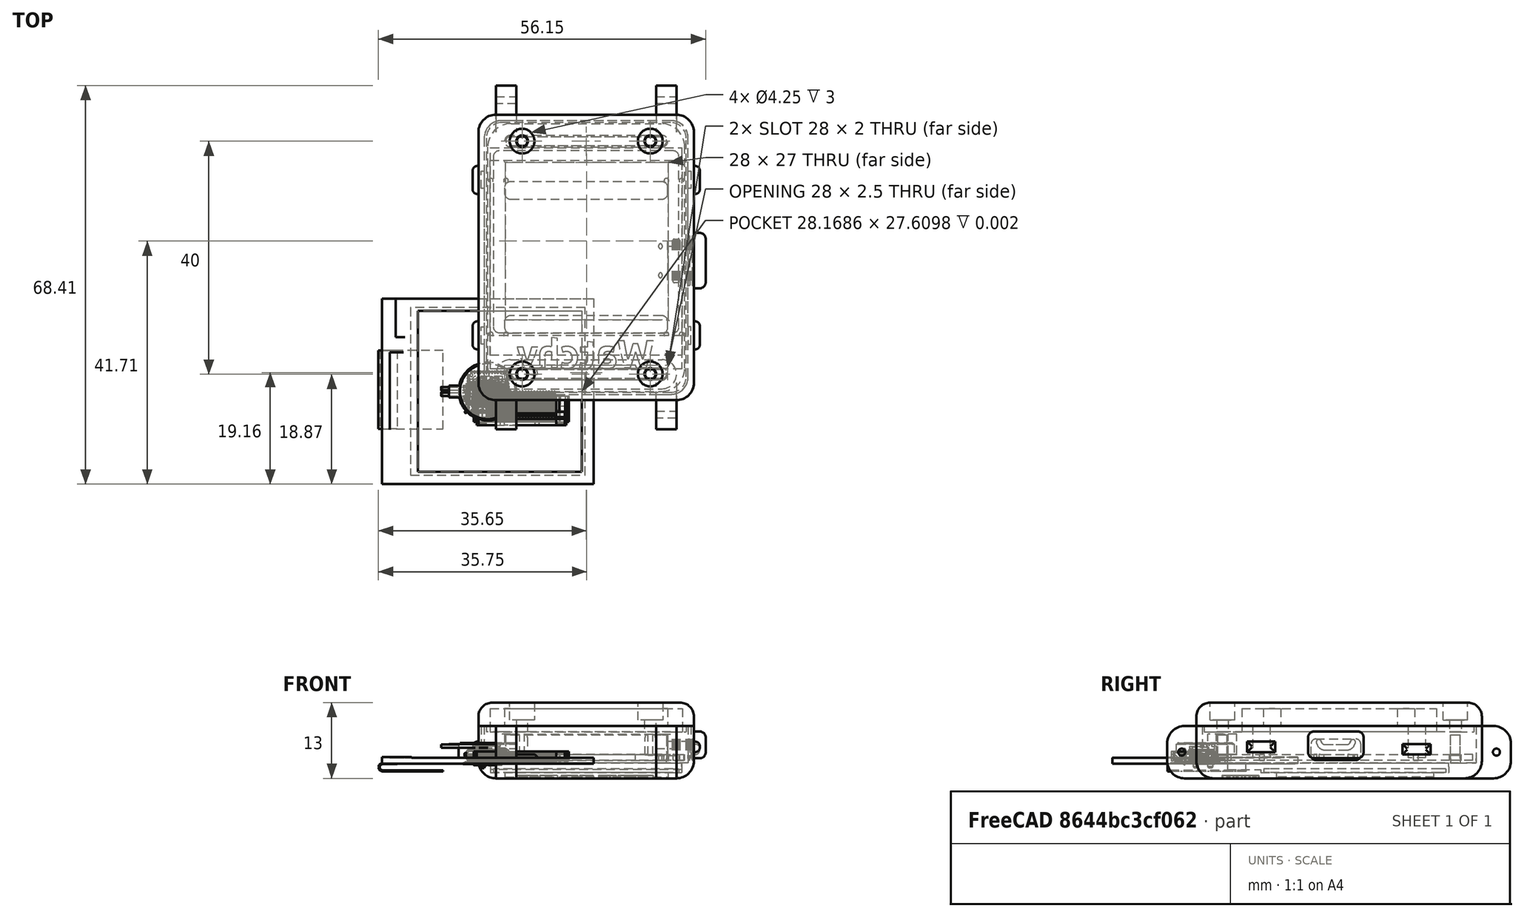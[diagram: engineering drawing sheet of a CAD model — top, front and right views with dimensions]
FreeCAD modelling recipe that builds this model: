
FCSTD DOCUMENT  (FreeCAD 0.20R29177 +426 (Git))
Label: JJ-WATCHY
License: All rights reserved
LicenseURL: http://en.wikipedia.org/wiki/All_rights_reserved
objects: Part::Feature×58, App::Part×56, Sketcher::SketchObject×26, PartDesign::Pad×21, PartDesign::Pocket×14, PartDesign::Fillet×10, PartDesign::ShapeBinder×7, PartDesign::Body×6, PartDesign::Plane×3, Part::Part2DObjectPython×1, Part::Extrusion×1, PartDesign::FeatureBase×1, Mesh::Feature×1, Part::Fuse×1, Part::Cut×1
note: 195 computed .brp shape members not serialized (recipe doc carries the construction recipe); baked Part::Feature solids carry a one-line shape summary decoded from their .brp

FEATURE [Part::Feature] Part__Feature  label="SOLID (15)"
  shape: bbox 7.981 x 5.422 x 2.941 mm, 498 faces (baked)
FEATURE [App::Part] USB_Micro_B_Molex_47346_0001  label="USB_Micro-B_Molex_47346-0001"
  Group = -> [Part__Feature]
  Origin = -> Origin
  Placement = pos=(31.38,22.43,1.65) rot=(0,0,1;1.5708rad)
FEATURE [Part::Feature] Part__Feature001  label="SOLID"
  shape: bbox 1.6 x 0.8 x 0.8 mm, 28 faces (baked)
FEATURE [App::Part] C_0603_1608Metric
  Group = -> [Part__Feature001]
  Origin = -> Origin001
  Placement = pos=(5.16,37.71,1.65) rot=(0,0,1;0rad)
FEATURE [Part::Feature] Part__Feature002  label="SOLID (16)"
  shape: bbox 6.669 x 4.906 x 2.452 mm, 452 faces (baked)
FEATURE [App::Part] Button
  Group = -> [Part__Feature002]
  Origin = -> Origin002
  Placement = pos=(2.38,35.43,1.65) rot=(0,0,-1;1.5708rad)
FEATURE [Part::Feature] Part__Feature003  label="SOLID (16)001"
  shape: bbox 6.669 x 4.906 x 2.452 mm, 452 faces (baked)
FEATURE [App::Part] Button001
  Group = -> [Part__Feature003]
  Origin = -> Origin003
  Placement = pos=(2.38,8.73,1.65) rot=(0,0,-1;1.5708rad)
FEATURE [Part::Feature] Part__Feature004  label="SOLID (16)002"
  shape: bbox 6.669 x 4.906 x 2.452 mm, 452 faces (baked)
FEATURE [App::Part] Button002
  Group = -> [Part__Feature004]
  Origin = -> Origin004
  Placement = pos=(31.42,37.23,1.65) rot=(0,0,1;1.5708rad)
FEATURE [Part::Feature] Part__Feature005  label="SOLID (16)003"
  shape: bbox 6.669 x 4.906 x 2.452 mm, 452 faces (baked)
FEATURE [App::Part] Button003
  Group = -> [Part__Feature005]
  Origin = -> Origin005
  Placement = pos=(31.42,10.53,1.65) rot=(0,0,1;1.5708rad)
FEATURE [Part::Feature] Part__Feature006  label="SOLID (1)"
  shape: bbox 2 x 2 x 1.025 mm, 68 faces (baked)
FEATURE [App::Part] LGA_12_2x2mm_P0_5mm  label="LGA-12_2x2mm_P0.5mm"
  Group = -> [Part__Feature006]
  Origin = -> Origin006
  Placement = pos=(10.76,34.89,1.65) rot=(0,0,1;3.14159rad)
FEATURE [Part::Feature] Part__Feature007  label="COMPOUND (3)"
  shape: bbox 16.3 x 5.85 x 2.11 mm, 1280 faces, 17 solids (baked)
FEATURE [App::Part] FPC_24  label="FPC-24"
  Group = -> [Part__Feature007]
  Origin = -> Origin007
  Placement = pos=(11.025,19.09,1.65) rot=(0,0,1;0rad)
FEATURE [Part::Feature] Part__Feature008  label="SOLID (4)"
  shape: bbox 7.65 x 5.2 x 3.4 mm, 136 faces (baked)
FEATURE [App::Part] Molex_PicoBlade_53261_0271_1x02_1MP_P1_25mm_Horizontal  label="Molex_PicoBlade_53261-0271_1x02-1MP_P1.25mm_Horizontal"
  Group = -> [Part__Feature008]
  Origin = -> Origin008
  Placement = pos=(28.63,31.39,1.65) rot=(0,0,-1;1.5708rad)
FEATURE [Part::Feature] Part__Feature009  label="SOLID (2)"
  shape: bbox 1 x 0.5 x 0.35 mm, 26 faces (baked)
FEATURE [App::Part] R_0402_1005Metric
  Group = -> [Part__Feature009]
  Origin = -> Origin009
  Placement = pos=(31.7,28.28,1.65) rot=(0,0,1;1.5708rad)
FEATURE [Part::Feature] Part__Feature010  label="SOLID (5)"
  shape: bbox 4 x 4 x 1.1 mm, 158 faces (baked)
FEATURE [App::Part] QFN_24_1EP_4x4mm_P0_5mm_EP2_7x2_7mm  label="QFN-24-1EP_4x4mm_P0.5mm_EP2.7x2.7mm"
  Group = -> [Part__Feature010]
  Origin = -> Origin010
  Placement = pos=(25.76,24.38,1.65) rot=(0,0,1;0rad)
FEATURE [Part::Feature] Part__Feature011  label="SOLID (2)001"
  shape: bbox 1 x 0.5 x 0.35 mm, 26 faces (baked)
FEATURE [App::Part] R_0402_1005Metric001
  Group = -> [Part__Feature011]
  Origin = -> Origin011
  Placement = pos=(29.05,13.07,1.65) rot=(0,0,1;0rad)
FEATURE [Part::Feature] Part__Feature012  label="SOLID001"
  shape: bbox 1.6 x 0.8 x 0.8 mm, 28 faces (baked)
FEATURE [App::Part] C_0603_1608Metric001
  Group = -> [Part__Feature012]
  Origin = -> Origin012
  Placement = pos=(21.71,23.42,1.65) rot=(0,0,1;0rad)
FEATURE [Part::Feature] Part__Feature013  label="COMPOUND"
  shape: bbox 37.16 x 32.08 x 2.7 mm, 57 faces, 2 solids (baked)
FEATURE [App::Part] Display
  Group = -> [Part__Feature013]
  Origin = -> Origin013
  Placement = pos=(16.89,23.15,0.55) rot=(0.707107,0.707107,0;3.14159rad)
FEATURE [Part::Feature] Part__Feature014  label="SOLID002"
  shape: bbox 1.6 x 0.8 x 0.8 mm, 28 faces (baked)
FEATURE [App::Part] C_0603_1608Metric002
  Group = -> [Part__Feature014]
  Origin = -> Origin014
  Placement = pos=(15.42,35.06,1.65) rot=(0,0,1;1.5708rad)
FEATURE [Part::Feature] Part__Feature015  label="SOLID003"
  shape: bbox 1.6 x 0.8 x 0.8 mm, 28 faces (baked)
FEATURE [App::Part] C_0603_1608Metric003
  Group = -> [Part__Feature015]
  Origin = -> Origin015
  Placement = pos=(19.01,21.47,1.65) rot=(0,0,1;1.5708rad)
FEATURE [Part::Feature] Part__Feature016  label="SOLID (3)"
  shape: bbox 2 x 1.25 x 1.25 mm, 28 faces (baked)
FEATURE [App::Part] C_0805_2012Metric
  Group = -> [Part__Feature016]
  Origin = -> Origin016
  Placement = pos=(5.63,12.59,1.65) rot=(0,0,1;0rad)
FEATURE [Part::Feature] Part__Feature017  label="SOLID (3)001"
  shape: bbox 2 x 1.25 x 1.25 mm, 28 faces (baked)
FEATURE [App::Part] C_0805_2012Metric001
  Group = -> [Part__Feature017]
  Origin = -> Origin017
  Placement = pos=(6.63,6.34,1.65) rot=(0,0,1;0rad)
FEATURE [Part::Feature] Part__Feature018  label="SOLID004"
  shape: bbox 1.6 x 0.8 x 0.8 mm, 28 faces (baked)
FEATURE [App::Part] C_0603_1608Metric004
  Group = -> [Part__Feature018]
  Origin = -> Origin018
  Placement = pos=(13.81,21.47,1.65) rot=(0,0,1;1.5708rad)
FEATURE [Part::Feature] Part__Feature019  label="SOLID005"
  shape: bbox 1.6 x 0.8 x 0.8 mm, 28 faces (baked)
FEATURE [App::Part] C_0603_1608Metric005
  Group = -> [Part__Feature019]
  Origin = -> Origin019
  Placement = pos=(16.41,21.47,1.65) rot=(0,0,1;1.5708rad)
FEATURE [Part::Feature] Part__Feature020  label="SOLID006"
  shape: bbox 1.6 x 0.8 x 0.8 mm, 28 faces (baked)
FEATURE [App::Part] C_0603_1608Metric006
  Group = -> [Part__Feature020]
  Origin = -> Origin020
  Placement = pos=(17.71,21.47,1.65) rot=(0,0,1;1.5708rad)
FEATURE [Part::Feature] Part__Feature021  label="SOLID007"
  shape: bbox 1.6 x 0.8 x 0.8 mm, 28 faces (baked)
FEATURE [App::Part] C_0603_1608Metric007
  Group = -> [Part__Feature021]
  Origin = -> Origin021
  Placement = pos=(15.11,21.47,1.65) rot=(0,0,1;1.5708rad)
FEATURE [Part::Feature] Part__Feature022  label="SOLID008"
  shape: bbox 1.6 x 0.8 x 0.8 mm, 28 faces (baked)
FEATURE [App::Part] C_0603_1608Metric008
  Group = -> [Part__Feature022]
  Origin = -> Origin022
  Placement = pos=(12.46,21.47,1.65) rot=(0,0,1;1.5708rad)
FEATURE [Part::Feature] Part__Feature023  label="SOLID009"
  shape: bbox 1.6 x 0.8 x 0.8 mm, 28 faces (baked)
FEATURE [App::Part] C_0603_1608Metric009
  Group = -> [Part__Feature023]
  Origin = -> Origin023
  Placement = pos=(11.16,21.47,1.65) rot=(0,0,1;1.5708rad)
FEATURE [Part::Feature] Part__Feature024  label="SOLID (3)002"
  shape: bbox 2 x 1.25 x 1.25 mm, 28 faces (baked)
FEATURE [App::Part] C_0805_2012Metric002
  Group = -> [Part__Feature024]
  Origin = -> Origin024
  Placement = pos=(17.82,35.53,1.65) rot=(0,0,1;3.14159rad)
FEATURE [Part::Feature] Part__Feature025  label="SOLID (6)"
  shape: bbox 3.8 x 1.6 x 1.25 mm, 67 faces (baked)
FEATURE [App::Part] D_SOD_123  label="D_SOD-123"
  Group = -> [Part__Feature025]
  Origin = -> Origin025
  Placement = pos=(1.25,15.82,1.65) rot=(0,0,1;1.5708rad)
FEATURE [Part::Feature] Part__Feature026  label="SOLID (6)001"
  shape: bbox 3.8 x 1.6 x 1.25 mm, 67 faces (baked)
FEATURE [App::Part] D_SOD_123001  label="D_SOD-124"
  Group = -> [Part__Feature026]
  Origin = -> Origin026
  Placement = pos=(3.55,15.82,1.65) rot=(0,0,-1;1.5708rad)
FEATURE [Part::Feature] Part__Feature027  label="SOLID (6)002"
  shape: bbox 3.8 x 1.6 x 1.25 mm, 67 faces (baked)
FEATURE [App::Part] D_SOD_123002  label="D_SOD-125"
  Group = -> [Part__Feature027]
  Origin = -> Origin027
  Placement = pos=(5.85,15.82,1.65) rot=(0,0,-1;1.5708rad)
FEATURE [Part::Feature] Part__Feature028  label="SOLID (6)003"
  shape: bbox 3.8 x 1.6 x 1.25 mm, 67 faces (baked)
FEATURE [App::Part] D_SOD_123003  label="D_SOD-126"
  Group = -> [Part__Feature028]
  Origin = -> Origin028
  Placement = pos=(27.27,19.28,1.65) rot=(0,0,1;1.5708rad)
FEATURE [Part::Feature] Part__Feature029  label="SOLID (7)"
  shape: bbox 1.6 x 0.8 x 1.1 mm, 50 faces (baked)
FEATURE [App::Part] LED_0603_1608Metric
  Group = -> [Part__Feature029]
  Origin = -> Origin029
  Placement = pos=(33.04,30.53,1.65) rot=(0,0,1;1.5708rad)
FEATURE [Part::Feature] Part__Feature030  label="SOLID (8)"
  shape: bbox 3.5 x 1.6 x 1.1 mm, 27 faces (baked)
FEATURE [App::Part] D_SOD_123F  label="D_SOD-123F"
  Group = -> [Part__Feature030]
  Origin = -> Origin030
  Placement = pos=(4.91,34.705,1.65) rot=(0,0,-1;1.5708rad)
FEATURE [Part::Feature] Part__Feature031  label="SOLID (9)"
  shape: bbox 3.2 x 2.5 x 2.5 mm, 28 faces (baked)
FEATURE [App::Part] L_1210_3225Metric
  Group = -> [Part__Feature031]
  Origin = -> Origin031
  Placement = pos=(6.13,9.47,1.65) rot=(0,0,-1;1.5708rad)
FEATURE [Part::Feature] Part__Feature032  label="SOLID (10)"
  shape: bbox 2.5 x 3 x 1.2 mm, 76 faces (baked)
FEATURE [App::Part] SOT_23  label="SOT-23"
  Group = -> [Part__Feature032]
  Origin = -> Origin032
  Placement = pos=(28.1,9.03,1.65) rot=(0,0,-1;1.5708rad)
FEATURE [Part::Feature] Part__Feature033  label="SOLID (10)001"
  shape: bbox 2.5 x 3 x 1.2 mm, 76 faces (baked)
FEATURE [App::Part] SOT_23001  label="SOT-024"
  Group = -> [Part__Feature033]
  Origin = -> Origin033
  Placement = pos=(28.45,15.23,1.65) rot=(0,0,-1;1.5708rad)
FEATURE [Part::Feature] Part__Feature034  label="SOLID (10)002"
  shape: bbox 2.5 x 3 x 1.2 mm, 76 faces (baked)
FEATURE [App::Part] SOT_23002  label="SOT-025"
  Group = -> [Part__Feature034]
  Origin = -> Origin034
  Placement = pos=(7.81,35.31,1.65) rot=(0,0,1;3.14159rad)
FEATURE [Part::Feature] Part__Feature035  label="SOLID (2)002"
  shape: bbox 1 x 0.5 x 0.35 mm, 26 faces (baked)
FEATURE [App::Part] R_0402_1005Metric002
  Group = -> [Part__Feature035]
  Origin = -> Origin035
  Placement = pos=(16.97,34.19,1.65) rot=(0,0,1;3.14159rad)
FEATURE [Part::Feature] Part__Feature036  label="SOLID (2)003"
  shape: bbox 1 x 0.5 x 0.35 mm, 26 faces (baked)
FEATURE [App::Part] R_0402_1005Metric003
  Group = -> [Part__Feature036]
  Origin = -> Origin036
  Placement = pos=(22.55,26.67,1.65) rot=(0,0,1;1.5708rad)
FEATURE [Part::Feature] Part__Feature037  label="SOLID (2)004"
  shape: bbox 1 x 0.5 x 0.35 mm, 26 faces (baked)
FEATURE [App::Part] R_0402_1005Metric004
  Group = -> [Part__Feature037]
  Origin = -> Origin037
  Placement = pos=(23.91,27.48,1.65) rot=(0,0,1;3.14159rad)
FEATURE [Part::Feature] Part__Feature038  label="SOLID (2)005"
  shape: bbox 1 x 0.5 x 0.35 mm, 26 faces (baked)
FEATURE [App::Part] R_0402_1005Metric005
  Group = -> [Part__Feature038]
  Origin = -> Origin038
  Placement = pos=(27.15,13.07,1.65) rot=(0,0,1;3.14159rad)
FEATURE [Part::Feature] Part__Feature039  label="SOLID (2)006"
  shape: bbox 1 x 0.5 x 0.35 mm, 26 faces (baked)
FEATURE [App::Part] R_0402_1005Metric006
  Group = -> [Part__Feature039]
  Origin = -> Origin039
  Placement = pos=(28.66,36.44,1.65) rot=(0,0,1;0rad)
FEATURE [Part::Feature] Part__Feature040  label="SOLID (2)007"
  shape: bbox 1 x 0.5 x 0.35 mm, 26 faces (baked)
FEATURE [App::Part] R_0402_1005Metric007
  Group = -> [Part__Feature040]
  Origin = -> Origin040
  Placement = pos=(6.69,32.68,1.65) rot=(0,0,-1;1.5708rad)
FEATURE [Part::Feature] Part__Feature041  label="SOLID (2)008"
  shape: bbox 1 x 0.5 x 0.35 mm, 26 faces (baked)
FEATURE [App::Part] R_0402_1005Metric008
  Group = -> [Part__Feature041]
  Origin = -> Origin041
  Placement = pos=(29.05,11.28,1.65) rot=(0,0,1;3.14159rad)
FEATURE [Part::Feature] Part__Feature042  label="SOLID (2)009"
  shape: bbox 1 x 0.5 x 0.35 mm, 26 faces (baked)
FEATURE [App::Part] R_0402_1005Metric009
  Group = -> [Part__Feature042]
  Origin = -> Origin042
  Placement = pos=(27.15,11.28,1.65) rot=(0,0,1;3.14159rad)
FEATURE [Part::Feature] Part__Feature043  label="SOLID (2)010"
  shape: bbox 1 x 0.5 x 0.35 mm, 26 faces (baked)
FEATURE [App::Part] R_0402_1005Metric010
  Group = -> [Part__Feature043]
  Origin = -> Origin043
  Placement = pos=(4.35,6.34,1.65) rot=(0,0,1;1.5708rad)
FEATURE [Part::Feature] Part__Feature044  label="SOLID (2)011"
  shape: bbox 1 x 0.5 x 0.35 mm, 26 faces (baked)
FEATURE [App::Part] R_0402_1005Metric011
  Group = -> [Part__Feature044]
  Origin = -> Origin044
  Placement = pos=(30.8,28.28,1.65) rot=(0,0,1;1.5708rad)
FEATURE [Part::Feature] Part__Feature045  label="SOLID (2)012"
  shape: bbox 1 x 0.5 x 0.35 mm, 26 faces (baked)
FEATURE [App::Part] R_0402_1005Metric012
  Group = -> [Part__Feature045]
  Origin = -> Origin045
  Placement = pos=(29.32,17.4,1.65) rot=(0,0,1;3.14159rad)
FEATURE [Part::Feature] Part__Feature046  label="SOLID (2)013"
  shape: bbox 1 x 0.5 x 0.35 mm, 26 faces (baked)
FEATURE [App::Part] R_0402_1005Metric013
  Group = -> [Part__Feature046]
  Origin = -> Origin046
  Placement = pos=(33.24,28.28,1.65) rot=(0,0,-1;1.5708rad)
FEATURE [Part::Feature] Part__Feature047  label="SOLID (2)014"
  shape: bbox 1 x 0.5 x 0.35 mm, 26 faces (baked)
FEATURE [App::Part] R_0402_1005Metric014
  Group = -> [Part__Feature047]
  Origin = -> Origin047
  Placement = pos=(7.75,32.68,1.65) rot=(0,0,-1;1.5708rad)
FEATURE [Part::Feature] Part__Feature048  label="SOLID (13)"
  shape: bbox 7 x 7 x 0.77 mm, 302 faces (baked)
FEATURE [App::Part] QFN_48_1EP_7x7mm_P0_5mm_EP5_15x5_15mm  label="QFN-48-1EP_7x7mm_P0.5mm_EP5.15x5.15mm"
  Group = -> [Part__Feature048]
  Origin = -> Origin048
  Placement = pos=(17.7737,29.6588,1.65) rot=(0,0,-1;1.5708rad)
FEATURE [Part::Feature] Part__Feature049  label="SOLID (11)"
  shape: bbox 2.8 x 2.9 x 1.55 mm, 109 faces (baked)
FEATURE [App::Part] SOT_23_5  label="SOT-23-5"
  Group = -> [Part__Feature049]
  Origin = -> Origin049
  Placement = pos=(24.66,19.88,1.65) rot=(0,0,-1;1.5708rad)
FEATURE [Part::Feature] Part__Feature050  label="SOLID (11)001"
  shape: bbox 2.8 x 2.9 x 1.55 mm, 109 faces (baked)
FEATURE [App::Part] SOT_23_5001  label="SOT-23-006"
  Group = -> [Part__Feature050]
  Origin = -> Origin050
  Placement = pos=(32,15.93,1.65) rot=(0,0,-1;1.5708rad)
FEATURE [Part::Feature] Part__Feature051  label="SOLID (12)"
  shape: bbox 2 x 2 x 1.05 mm, 118 faces (baked)
FEATURE [App::Part] SOT_363_SC_70_6  label="SOT-363_SC-70-6"
  Group = -> [Part__Feature051]
  Origin = -> Origin051
  Placement = pos=(21.31,21.47,1.65) rot=(0,0,1;3.14159rad)
FEATURE [Part::Feature] Part__Feature052  label="SOLID (14)"
  shape: bbox 6 x 4.9 x 1.75 mm, 156 faces (baked)
FEATURE [App::Part] SOIC_8_3_9x4_9mm_P1_27mm  label="SOIC-8_3.9x4.9mm_P1.27mm"
  Group = -> [Part__Feature052]
  Origin = -> Origin052
  Placement = pos=(11.07,29.81,1.65) rot=(0,0,1;1.5708rad)
FEATURE [Part::Feature] Part__Feature053  label="SOLID (2)015"
  shape: bbox 1 x 0.5 x 0.35 mm, 26 faces (baked)
FEATURE [App::Part] R_0402_1005Metric015
  Group = -> [Part__Feature053]
  Origin = -> Origin053
  Placement = pos=(7.75,30.52,1.65) rot=(0,0,-1;1.5708rad)
FEATURE [Part::Feature] Part__Feature054  label="COMPOUND (1)"
  shape: bbox 13 x 10 x 2.5 mm, 15 faces, 3 solids (baked)
FEATURE [App::Part] PagerMotor
  Group = -> [Part__Feature054]
  Origin = -> Origin054
  Placement = pos=(5.45,22.955,5.15) rot=(0.819152,-0.573576,0;3.14159rad)
FEATURE [Part::Feature] Part__Feature055  label="COMPOUND (2)"
  shape: bbox 33.8 x 45.96 x 1 mm, 46 faces (baked)
FEATURE [App::Part] Watchy_Fixed_Dimensions_v1  label="Watchy Fixed Dimensions v1"
  Group = -> [USB_Micro_B_Molex_47346_0001,C_0603_1608Metric,Button,Button001,Button002,Button003,LGA_12_2x2mm_P0_5mm,FPC_24,Molex_PicoBlade_53261_0271_1x02_1MP_P1_25mm_Horizontal,R_0402_1005Metric,QFN_24_1EP_4x4mm_P0_5mm_EP2_7x2_7mm,R_0402_1005Metric001,C_0603_1608Metric001,Display,C_0603_1608Metric002,C_0603_1608Metric003,C_0805_2012Metric,C_0805_2012Metric001,C_0603_1608Metric004,C_0603_1608Metric005,+36 more]
  Origin = -> Origin055
  Placement = pos=(0,0,-0.43) rot=(0,0,1;0rad)
FEATURE [Sketcher::SketchObject] Sketch
  FullyConstrained = true
  MapMode = 5
  Placement = pos=(0,0,0) rot=(0,1,0;3.14159rad)
  Support = -> [XY_Plane056]
  sketch-geometry (4):
    g0: LineSegment StartX=-32.81 StartY=41.31 StartZ=0 EndX=-0.98 EndY=41.31 EndZ=0
    g1: LineSegment StartX=-0.98 StartY=41.31 StartZ=0 EndX=-0.98 EndY=10.07 EndZ=0
    g2: LineSegment StartX=-0.98 StartY=10.07 StartZ=0 EndX=-32.81 EndY=10.07 EndZ=0
    g3: LineSegment StartX=-32.81 StartY=10.07 StartZ=0 EndX=-32.81 EndY=41.31 EndZ=0
  constraints (12):
    c: Coincident(g0,g1)
    c: Coincident(g1,g2)
    c: Coincident(g2,g3)
    c: Coincident(g3,g0)
    c: Horizontal(g0)
    c: Horizontal(g2)
    c: Vertical(g1)
    c: Vertical(g3)
    c: DistanceX(g0,g0) = 31.83
    c: DistanceY(g1,g1) = 31.24
    c: DistanceY(g-1,g1) = 10.07
    c: DistanceX(g1,g-1) = 0.98
FEATURE [PartDesign::Pad] Pad
  Direction = (0,0,-1)
  Length = 1.5
  Length2 = 10
  Profile = -> Sketch
  ReferenceAxis = -> Sketch [N_Axis]
  Type = 0
FEATURE [PartDesign::Fillet] Fillet
  Base = -> Pad [Edge1,Edge2,Edge5,Edge8]
  BaseFeature = -> Pad
  Radius = 1
  SupportTransform = false
  UseAllEdges = false
FEATURE [PartDesign::Pocket] Pocket
  BaseFeature = -> Fillet
  Direction = (0,0,-1)
  Length = 0.9
  Length2 = 5
  Profile = -> Fillet [Face2]
  Type = 0
FEATURE [PartDesign::ShapeBinder] ReferencePocket
  Placement = pos=(0,0,-1.5) rot=(0,0,1;0rad)
  Support = -> [Pocket]
  TraceSupport = false
FEATURE [PartDesign::Plane] DatumPlane
  Length = 75.1964
  MapMode = 5
  Placement = pos=(0,0,-1.5) rot=(1,0,0;3.14159rad)
  ResizeMode = 0
  Support = -> [ReferencePocket]
  Width = 91.2964
FEATURE [Sketcher::SketchObject] Sketch001
  ExternalGeometry = -> [ReferencePocket]
  FullyConstrained = true
  MapMode = 5
  Placement = pos=(0,0,-1.5) rot=(1,0,0;3.14159rad)
  Support = -> [DatumPlane]
  sketch-geometry (5):
    g0: LineSegment StartX=-1.6 StartY=1.5 StartZ=0 EndX=35.4 EndY=1.5 EndZ=0
    g1: LineSegment StartX=35.4 StartY=1.5 StartZ=0 EndX=35.4 EndY=-47.5 EndZ=0
    g2: LineSegment StartX=35.4 StartY=-47.5 StartZ=0 EndX=-1.6 EndY=-47.5 EndZ=0
    g3: LineSegment StartX=-1.6 StartY=-47.5 StartZ=0 EndX=-1.6 EndY=1.5 EndZ=0
    g4: GeomPoint X=16.9 Y=-23 Z=0
  constraints (13):
    c: Coincident(g0,g1)
    c: Coincident(g1,g2)
    c: Coincident(g2,g3)
    c: Coincident(g3,g0)
    c: Horizontal(g0)
    c: Horizontal(g2)
    c: Vertical(g1)
    c: Vertical(g3)
    c: DistanceX(g0,g0) = 37
    c: DistanceY(g1,g1) = 49
    c: DistanceX(g-1,g4) = 16.9
    c: DistanceY(g4,g-1) = 23
    c: Symmetric(g2,g0,g4)
FEATURE [PartDesign::Pad] Pad001
  Direction = (0,0,-1)
  Length = 1
  Length2 = 8
  Placement = pos=(0,0,-1.5) rot=(1,0,0;3.14159rad)
  Profile = -> Sketch001
  ReferenceAxis = -> Sketch001 [N_Axis]
  Type = 4
FEATURE [Sketcher::SketchObject] Sketch002
  FullyConstrained = true
  MapMode = 5
  Placement = pos=(0,0,-2.5) rot=(1,0,0;3.14159rad)
  Support = -> [Pad001]
  sketch-geometry (5):
    g0: LineSegment StartX=3 StartY=-12.3 StartZ=0 EndX=31 EndY=-12.3 EndZ=0
    g1: LineSegment StartX=31 StartY=-12.3 StartZ=0 EndX=31 EndY=-39.3 EndZ=0
    g2: LineSegment StartX=31 StartY=-39.3 StartZ=0 EndX=3 EndY=-39.3 EndZ=0
    g3: LineSegment StartX=3 StartY=-39.3 StartZ=0 EndX=3 EndY=-12.3 EndZ=0
    g4: GeomPoint X=17 Y=-25.8 Z=0
  constraints (13):
    c: Coincident(g0,g1)
    c: Coincident(g1,g2)
    c: Coincident(g2,g3)
    c: Coincident(g3,g0)
    c: Horizontal(g0)
    c: Horizontal(g2)
    c: Vertical(g1)
    c: Vertical(g3)
    c: DistanceX(g0,g0) = 28
    c: DistanceY(g1,g1) = 27
    c: DistanceX(g-1,g4) = 17
    c: DistanceY(g4,g-1) = 25.8
    c: Symmetric(g2,g0,g4)
FEATURE [PartDesign::Pocket] Pocket001
  BaseFeature = -> Pad001
  Direction = (0,-1e-16,1)
  Length = 1
  Length2 = 5
  Placement = pos=(0,0,-1.5) rot=(1,0,0;3.14159rad)
  Profile = -> Sketch002
  ReferenceAxis = -> Sketch002 [N_Axis]
  Type = 0
FEATURE [Sketcher::SketchObject] Sketch003
  ExternalGeometry = -> [Pocket001]
  FullyConstrained = true
  MapMode = 5
  Placement = pos=(0,0,6.5) rot=(0,0,1;0rad)
  Support = -> [Pocket001]
  sketch-geometry (5):
    g0: LineSegment StartX=-0.6 StartY=46.5 StartZ=0 EndX=-0.6 EndY=-0.5 EndZ=0
    g1: LineSegment StartX=-0.6 StartY=-0.5 StartZ=0 EndX=34.4 EndY=-0.5 EndZ=0
    g2: LineSegment StartX=34.4 StartY=-0.5 StartZ=0 EndX=34.4 EndY=46.5 EndZ=0
    g3: LineSegment StartX=34.4 StartY=46.5 StartZ=0 EndX=-0.6 EndY=46.5 EndZ=0
    g4: Circle CenterX=16.9 CenterY=23 CenterZ=0 NormalX=0 NormalY=0 NormalZ=1 AngleXU=0 Radius=29.3002
  constraints (14):
    c: Coincident(g0,g1)
    c: Coincident(g1,g2)
    c: Coincident(g2,g3)
    c: Coincident(g3,g0)
    c: PointOnObject(g0,g4)
    c: PointOnObject(g1,g4)
    c: PointOnObject(g2,g4)
    c: PointOnObject(g3,g4)
    c: Horizontal(g3)
    c: Horizontal(g1)
    c: Vertical(g2)
    c: DistanceX(g3,g3) = 35
    c: DistanceY(g2,g2) = 47
    c: Symmetric(g-3,g-4,g4)
FEATURE [PartDesign::Pocket] Pocket002
  BaseFeature = -> Pocket001
  Direction = (0,2e-16,-1)
  Length = 7
  Length2 = 5
  Placement = pos=(0,0,-1.5) rot=(1,0,0;3.14159rad)
  Profile = -> Sketch003
  ReferenceAxis = -> Sketch003 [N_Axis]
  Type = 0
FEATURE [Sketcher::SketchObject] Sketch004
  ExternalGeometry = -> [ReferencePocket]
  FullyConstrained = true
  MapMode = 5
  Placement = pos=(0,-2e-16,-0.5) rot=(0,0,1;0rad)
  Support = -> [Pocket002]
  sketch-geometry (4):
    g0: LineSegment StartX=0.48 StartY=41.81 StartZ=0 EndX=33.31 EndY=41.81 EndZ=0
    g1: LineSegment StartX=33.31 StartY=41.81 StartZ=0 EndX=33.31 EndY=9.57 EndZ=0
    g2: LineSegment StartX=33.31 StartY=9.57 StartZ=0 EndX=0.48 EndY=9.57 EndZ=0
    g3: LineSegment StartX=0.48 StartY=9.57 StartZ=0 EndX=0.48 EndY=41.81 EndZ=0
  constraints (12):
    c: Coincident(g0,g1)
    c: Coincident(g1,g2)
    c: Coincident(g2,g3)
    c: Coincident(g3,g0)
    c: Horizontal(g0)
    c: Horizontal(g2)
    c: Vertical(g1)
    c: Vertical(g3)
    c: DistanceX(g0,g-4) = 0.5
    c: DistanceX(g-6,g0) = 0.5
    c: DistanceY(g-3,g0) = 0.5
    c: DistanceY(g1,g-5) = 0.5
FEATURE [PartDesign::Pocket] Pocket003
  BaseFeature = -> Pocket002
  Direction = (0,4e-16,-1)
  Length = 1
  Length2 = 5
  Placement = pos=(0,0,-1.5) rot=(1,0,0;3.14159rad)
  Profile = -> Sketch004
  ReferenceAxis = -> Sketch004 [N_Axis]
  Type = 0
FEATURE [Sketcher::SketchObject] Sketch005
  FullyConstrained = true
  MapMode = 5
  Placement = pos=(34.4,0,-1.5) rot=(0.57735,0.57735,-0.57735;4.18879rad)
  Support = -> [Pocket003]
  sketch-geometry (4):
    g0: LineSegment StartX=18.2 StartY=-2.15 StartZ=0 EndX=26.7 EndY=-2.15 EndZ=0
    g1: LineSegment StartX=26.7 StartY=-2.15 StartZ=0 EndX=26.7 EndY=-5.75 EndZ=0
    g2: LineSegment StartX=26.7 StartY=-5.75 StartZ=0 EndX=18.2 EndY=-5.75 EndZ=0
    g3: LineSegment StartX=18.2 StartY=-5.75 StartZ=0 EndX=18.2 EndY=-2.15 EndZ=0
  constraints (12):
    c: Coincident(g0,g1)
    c: Coincident(g1,g2)
    c: Coincident(g2,g3)
    c: Coincident(g3,g0)
    c: Horizontal(g0)
    c: Horizontal(g2)
    c: Vertical(g1)
    c: Vertical(g3)
    c: DistanceX(g2,g2) = 8.5
    c: DistanceY(g1,g1) = 3.6
    c: DistanceX(g-1,g0) = 18.2
    c: DistanceY(g0,g-1) = 2.15
FEATURE [PartDesign::Pocket] Pocket004
  BaseFeature = -> Pocket003
  Direction = (1,0,0)
  Length = 5
  Length2 = 5
  Placement = pos=(0,0,-1.5) rot=(1,0,0;3.14159rad)
  Profile = -> Sketch005
  ReferenceAxis = -> Sketch005 [N_Axis]
  Type = 0
FEATURE [Sketcher::SketchObject] Sketch006
  ExternalGeometry = -> [Pocket004]
  FullyConstrained = true
  MapMode = 5
  Placement = pos=(0,0,6.5) rot=(0,0,1;0rad)
  Support = -> [Pocket004]
  sketch-geometry (20):
    g0: LineSegment StartX=-1.1 StartY=37.83 StartZ=0 EndX=-0.6 EndY=37.83 EndZ=0
    g1: LineSegment StartX=-0.6 StartY=37.83 StartZ=0 EndX=-0.6 EndY=34.83 EndZ=0
    g2: LineSegment StartX=-0.6 StartY=34.83 StartZ=0 EndX=-1.1 EndY=34.83 EndZ=0
    g3: LineSegment StartX=-1.1 StartY=34.83 StartZ=0 EndX=-1.1 EndY=37.83 EndZ=0
    g4: LineSegment StartX=34.4 StartY=37.83 StartZ=0 EndX=34.9 EndY=37.83 EndZ=0
    g5: LineSegment StartX=34.9 StartY=37.83 StartZ=0 EndX=34.9 EndY=34.83 EndZ=0
    g6: LineSegment StartX=34.9 StartY=34.83 StartZ=0 EndX=34.4 EndY=34.83 EndZ=0
    g7: LineSegment StartX=34.4 StartY=34.83 StartZ=0 EndX=34.4 EndY=37.83 EndZ=0
    g8: LineSegment StartX=34.4 StartY=8.13 StartZ=0 EndX=34.9 EndY=8.13 EndZ=0
    g9: LineSegment StartX=34.9 StartY=8.13 StartZ=0 EndX=34.9 EndY=11.13 EndZ=0
    g10: LineSegment StartX=34.9 StartY=11.13 StartZ=0 EndX=34.4 EndY=11.13 EndZ=0
    g11: LineSegment StartX=34.4 StartY=11.13 StartZ=0 EndX=34.4 EndY=8.13 EndZ=0
    g12: LineSegment StartX=-1.1 StartY=11.13 StartZ=0 EndX=-0.6 EndY=11.13 EndZ=0
    g13: LineSegment StartX=-0.6 StartY=11.13 StartZ=0 EndX=-0.6 EndY=8.13 EndZ=0
    g14: LineSegment StartX=-0.6 StartY=8.13 StartZ=0 EndX=-1.1 EndY=8.13 EndZ=0
    g15: LineSegment StartX=-1.1 StartY=8.13 StartZ=0 EndX=-1.1 EndY=11.13 EndZ=0
    g16: Circle CenterX=-0.85 CenterY=9.63 CenterZ=0 NormalX=0 NormalY=0 NormalZ=1 AngleXU=0 Radius=1.52069
    g17: Circle CenterX=34.65 CenterY=9.63 CenterZ=0 NormalX=0 NormalY=0 NormalZ=1 AngleXU=0 Radius=1.52069
    g18: Circle CenterX=34.65 CenterY=36.33 CenterZ=0 NormalX=0 NormalY=0 NormalZ=1 AngleXU=0 Radius=1.52069
    g19: Circle CenterX=-0.85 CenterY=36.33 CenterZ=0 NormalX=0 NormalY=0 NormalZ=1 AngleXU=0 Radius=1.52069
  constraints (60):
    c: Coincident(g0,g1)
    c: Coincident(g1,g2)
    c: Coincident(g2,g3)
    c: Coincident(g3,g0)
    c: Horizontal(g0)
    c: Horizontal(g2)
    c: Vertical(g1)
    c: Vertical(g3)
    c: PointOnObject(g0,g-3)
    c: DistanceX(g0,g0) = 0.5
    c: DistanceY(g3,g3) = 3
    c: Coincident(g4,g5)
    c: Coincident(g5,g6)
    c: Coincident(g6,g7)
    c: Coincident(g7,g4)
    c: Horizontal(g4)
    c: Horizontal(g6)
    c: Vertical(g5)
    c: Vertical(g7)
    c: Coincident(g8,g9)
    c: Coincident(g9,g10)
    c: Coincident(g10,g11)
    c: Coincident(g11,g8)
    c: Horizontal(g8)
    c: Horizontal(g10)
    c: Vertical(g9)
    c: Vertical(g11)
    c: Coincident(g12,g13)
    c: Coincident(g13,g14)
    c: Coincident(g14,g15)
    c: Coincident(g15,g12)
    c: Horizontal(g12)
    c: Horizontal(g14)
    c: Vertical(g13)
    c: Vertical(g15)
    c: Equal(g0,g12)
    c: Equal(g12,g4)
    c: Equal(g4,g8)
    c: Equal(g3,g13)
    c: Equal(g13,g5)
    c: Equal(g5,g9)
    c: PointOnObject(g12,g-3)
    c: PointOnObject(g4,g-4)
    c: PointOnObject(g8,g-4)
    c: PointOnObject(g12,g16)
    c: PointOnObject(g12,g16)
    c: PointOnObject(g14,g16)
    c: DistanceY(g-1,g16) = 9.63
    c: PointOnObject(g9,g17)
    c: PointOnObject(g10,g17)
    c: PointOnObject(g8,g17)
    c: PointOnObject(g4,g18)
    c: PointOnObject(g4,g18)
    c: PointOnObject(g5,g18)
    c: PointOnObject(g0,g19)
    c: PointOnObject(g0,g19)
    c: PointOnObject(g2,g19)
    c: DistanceY(g-1,g19) = 36.33
    c: DistanceY(g-1,g18) = 36.33
    c: DistanceY(g-1,g17) = 9.63
FEATURE [PartDesign::Pocket] Pocket005
  BaseFeature = -> Pocket004
  Direction = (0,0,-1)
  Length = 5.5
  Length2 = 5
  Placement = pos=(0,0,-1.5) rot=(1,0,0;3.14159rad)
  Profile = -> Sketch006
  ReferenceAxis = -> Sketch006 [N_Axis]
  Type = 0
FEATURE [Sketcher::SketchObject] Sketch007
  FullyConstrained = true
  MapMode = 5
  Placement = pos=(-1.6,0,-1.5) rot=(0.57735,0.57735,-0.57735;4.18879rad)
  Support = -> [Pocket005]
  sketch-geometry (8):
    g0: LineSegment StartX=7.23 StartY=-3.5 StartZ=0 EndX=12.03 EndY=-3.5 EndZ=0
    g1: LineSegment StartX=12.03 StartY=-3.5 StartZ=0 EndX=12.03 EndY=-5.3 EndZ=0
    g2: LineSegment StartX=12.03 StartY=-5.3 StartZ=0 EndX=7.23 EndY=-5.3 EndZ=0
    g3: LineSegment StartX=7.23 StartY=-5.3 StartZ=0 EndX=7.23 EndY=-3.5 EndZ=0
    g4: LineSegment StartX=33.9 StartY=-3.1 StartZ=0 EndX=38.7 EndY=-3.1 EndZ=0
    g5: LineSegment StartX=38.7 StartY=-3.1 StartZ=0 EndX=38.7 EndY=-4.9 EndZ=0
    g6: LineSegment StartX=38.7 StartY=-4.9 StartZ=0 EndX=33.9 EndY=-4.9 EndZ=0
    g7: LineSegment StartX=33.9 StartY=-4.9 StartZ=0 EndX=33.9 EndY=-3.1 EndZ=0
  constraints (24):
    c: Coincident(g0,g1)
    c: Coincident(g1,g2)
    c: Coincident(g2,g3)
    c: Coincident(g3,g0)
    c: Horizontal(g0)
    c: Horizontal(g2)
    c: Vertical(g1)
    c: Vertical(g3)
    c: Coincident(g4,g5)
    c: Coincident(g5,g6)
    c: Coincident(g6,g7)
    c: Coincident(g7,g4)
    c: Horizontal(g4)
    c: Horizontal(g6)
    c: Vertical(g5)
    c: Vertical(g7)
    c: DistanceX(g2,g2) = 4.8
    c: DistanceY(g1,g1) = 1.8
    c: Equal(g1,g7)
    c: Equal(g2,g6)
    c: DistanceY(g0,g-1) = 3.5
    c: DistanceY(g4,g-1) = 3.1
    c: DistanceX(g-1,g0) = 7.23
    c: DistanceX(g-1,g4) = 33.9
FEATURE [PartDesign::Pad] Pad002
  BaseFeature = -> Pocket005
  Direction = (-1,0,0)
  Length = 1
  Length2 = 10
  Placement = pos=(0,0,-1.5) rot=(1,0,0;3.14159rad)
  Profile = -> Sketch007
  ReferenceAxis = -> Sketch007 [N_Axis]
  Type = 0
FEATURE [Sketcher::SketchObject] Sketch008
  ExternalGeometry = -> [Pad002]
  FullyConstrained = true
  MapMode = 5
  Placement = pos=(35.4,0,-1.5) rot=(0.57735,-0.57735,0.57735;4.18879rad)
  Support = -> [Pad002]
  sketch-geometry (8):
    g0: LineSegment StartX=-12.03 StartY=-3.5 StartZ=0 EndX=-7.23 EndY=-3.5 EndZ=0
    g1: LineSegment StartX=-7.23 StartY=-3.5 StartZ=0 EndX=-7.23 EndY=-5.3 EndZ=0
    g2: LineSegment StartX=-7.23 StartY=-5.3 StartZ=0 EndX=-12.03 EndY=-5.3 EndZ=0
    g3: LineSegment StartX=-12.03 StartY=-5.3 StartZ=0 EndX=-12.03 EndY=-3.5 EndZ=0
    g4: LineSegment StartX=-38.7 StartY=-3.1 StartZ=0 EndX=-33.9 EndY=-3.1 EndZ=0
    g5: LineSegment StartX=-33.9 StartY=-3.1 StartZ=0 EndX=-33.9 EndY=-4.9 EndZ=0
    g6: LineSegment StartX=-33.9 StartY=-4.9 StartZ=0 EndX=-38.7 EndY=-4.9 EndZ=0
    g7: LineSegment StartX=-38.7 StartY=-4.9 StartZ=0 EndX=-38.7 EndY=-3.1 EndZ=0
  constraints (20):
    c: Coincident(g0,g1)
    c: Coincident(g1,g2)
    c: Coincident(g2,g3)
    c: Coincident(g3,g0)
    c: Horizontal(g0)
    c: Horizontal(g2)
    c: Vertical(g1)
    c: Vertical(g3)
    c: Coincident(g0,g-4)
    c: Coincident(g1,g-6)
    c: Coincident(g4,g5)
    c: Coincident(g5,g6)
    c: Coincident(g6,g7)
    c: Coincident(g7,g4)
    c: Horizontal(g4)
    c: Horizontal(g6)
    c: Vertical(g5)
    c: Vertical(g7)
    c: Coincident(g4,g-8)
    c: Coincident(g5,g-7)
FEATURE [PartDesign::Pad] Pad003
  BaseFeature = -> Pad002
  Direction = (1,0,0)
  Length = 1
  Length2 = 10
  Placement = pos=(0,0,-1.5) rot=(1,0,0;3.14159rad)
  Profile = -> Sketch008
  ReferenceAxis = -> Sketch008 [N_Axis]
  Type = 0
FEATURE [PartDesign::Fillet] Fillet001
  Base = -> Pad003 [Edge5,Edge105,Edge18,Edge124,Edge1,Edge2,Edge116,Edge103]
  BaseFeature = -> Pad003
  Placement = pos=(0,0,-1.5) rot=(1,0,0;3.14159rad)
  Radius = 3
  SupportTransform = false
  UseAllEdges = false
FEATURE [PartDesign::Fillet] Fillet002
  Base = -> Fillet001 [Edge41]
  BaseFeature = -> Fillet001
  Placement = pos=(0,0,-1.5) rot=(1,0,0;3.14159rad)
  Radius = 3
  SupportTransform = false
  UseAllEdges = false
FEATURE [PartDesign::Fillet] Fillet003
  Base = -> Fillet002 [Edge60,Edge59,Edge58,Edge61]
  BaseFeature = -> Fillet002
  Placement = pos=(0,0,-1.5) rot=(1,0,0;3.14159rad)
  Radius = 0.2
  SupportTransform = false
  UseAllEdges = false
FEATURE [PartDesign::ShapeBinder] ReferenceFillet003
  Placement = pos=(0,0,-1.5) rot=(1,0,0;3.14159rad)
  Support = -> [Fillet003]
  TraceSupport = false
FEATURE [PartDesign::Plane] DatumPlane001
  Length = 73.6348
  MapMode = 5
  Placement = pos=(0,0,6.5) rot=(0,0,1;0rad)
  ResizeMode = 0
  Support = -> [ReferenceFillet003]
  Width = 85.7348
FEATURE [Sketcher::SketchObject] Sketch009
  ExternalGeometry = -> [ReferenceFillet003]
  FullyConstrained = true
  MapMode = 5
  Placement = pos=(0,0,6.5) rot=(0,0,1;0rad)
  Support = -> [DatumPlane001]
  sketch-geometry (8):
    g0: LineSegment StartX=1.4 StartY=47.5 StartZ=0 EndX=32.4 EndY=47.5 EndZ=0
    g1: LineSegment StartX=-1.6 StartY=44.5 StartZ=0 EndX=-1.6 EndY=1.5 EndZ=0
    g2: LineSegment StartX=35.4 StartY=44.5 StartZ=0 EndX=35.4 EndY=1.5 EndZ=0
    g3: LineSegment StartX=1.4 StartY=-1.5 StartZ=0 EndX=32.4 EndY=-1.5 EndZ=0
    g4: ArcOfCircle CenterX=1.4 CenterY=1.5 CenterZ=0 NormalX=0 NormalY=0 NormalZ=1 AngleXU=0 Radius=3 StartAngle=3.14159 EndAngle=4.71239
    g5: ArcOfCircle CenterX=32.4 CenterY=1.5 CenterZ=0 NormalX=0 NormalY=0 NormalZ=1 AngleXU=0 Radius=3 StartAngle=4.71239 EndAngle=6.28319
    g6: ArcOfCircle CenterX=1.4 CenterY=44.5 CenterZ=0 NormalX=0 NormalY=0 NormalZ=1 AngleXU=0 Radius=3 StartAngle=1.5708 EndAngle=3.14159
    g7: ArcOfCircle CenterX=32.4 CenterY=44.5 CenterZ=0 NormalX=0 NormalY=0 NormalZ=1 AngleXU=0 Radius=3 StartAngle=3e-16 EndAngle=1.5708
  constraints (20):
    c: Coincident(g0,g-4)
    c: Coincident(g0,g-6)
    c: Coincident(g1,g-5)
    c: Coincident(g1,g-7)
    c: Coincident(g2,g-10)
    c: Coincident(g2,g-10)
    c: Coincident(g3,g-8)
    c: Coincident(g3,g-9)
    c: Coincident(g4,g-7)
    c: Coincident(g4,g1)
    c: Coincident(g4,g3)
    c: Coincident(g5,g-9)
    c: Coincident(g5,g2)
    c: Coincident(g5,g3)
    c: Coincident(g6,g-4)
    c: Coincident(g6,g1)
    c: Coincident(g6,g0)
    c: Coincident(g7,g-6)
    c: Coincident(g7,g0)
    c: Coincident(g7,g2)
FEATURE [PartDesign::Pad] Pad004
  Direction = (0,-4e-16,1)
  Length = 4
  Length2 = 10
  Placement = pos=(0,-2.9e-15,6.5) rot=(0,0,1;0rad)
  Profile = -> Sketch009
  ReferenceAxis = -> Sketch009 [N_Axis]
  Type = 0
FEATURE [PartDesign::Fillet] Fillet004
  Base = -> Pad004 [Edge7]
  BaseFeature = -> Pad004
  Placement = pos=(0,-2.9e-15,6.5) rot=(0,0,1;0rad)
  Radius = 2.4
  SupportTransform = false
  UseAllEdges = false
FEATURE [Sketcher::SketchObject] Sketch010
  ExternalGeometry = -> [ReferenceFillet003]
  FullyConstrained = true
  MapMode = 5
  Placement = pos=(0,-2.9e-15,6.5) rot=(1,0,0;3.14159rad)
  Support = -> [Fillet004]
  sketch-geometry (8):
    g0: ArcOfCircle CenterX=2.4 CenterY=-2.5 CenterZ=0 NormalX=0 NormalY=0 NormalZ=1 AngleXU=0 Radius=2 StartAngle=1.5708 EndAngle=3.14159
    g1: ArcOfCircle CenterX=31.4 CenterY=-2.5 CenterZ=0 NormalX=0 NormalY=0 NormalZ=1 AngleXU=0 Radius=2 StartAngle=0 EndAngle=1.5708
    g2: ArcOfCircle CenterX=31.4 CenterY=-43.5 CenterZ=0 NormalX=0 NormalY=0 NormalZ=1 AngleXU=0 Radius=2 StartAngle=4.71239 EndAngle=6.28319
    g3: ArcOfCircle CenterX=2.4 CenterY=-43.5 CenterZ=0 NormalX=0 NormalY=0 NormalZ=1 AngleXU=0 Radius=2 StartAngle=3.14159 EndAngle=4.7124
    g4: LineSegment StartX=0.4 StartY=-2.5 StartZ=0 EndX=0.4 EndY=-43.5 EndZ=0
    g5: LineSegment StartX=2.4 StartY=-0.5 StartZ=0 EndX=31.4 EndY=-0.5 EndZ=0
    g6: LineSegment StartX=33.4 StartY=-2.5 StartZ=0 EndX=33.4 EndY=-43.5 EndZ=0
    g7: LineSegment StartX=31.4 StartY=-45.5 StartZ=0 EndX=2.40002 EndY=-45.5 EndZ=0
  constraints (17):
    c: Coincident(g7,g3)
    c: Vertical(g6)
    c: Horizontal(g5)
    c: Vertical(g4)
    c: Horizontal(g7)
    c: DistanceX(g-6,g3) = 1
    c: Coincident(g3,g-6)
    c: Coincident(g0,g-5)
    c: Coincident(g1,g-4)
    c: Coincident(g2,g-3)
    c: Tangent(g4,g3) = -1.5708
    c: Tangent(g4,g0) = -1.5708
    c: Tangent(g5,g0) = 1.5708
    c: Tangent(g5,g1) = 1.5708
    c: Tangent(g6,g1) = 1.5708
    c: Tangent(g6,g2) = 1.5708
    c: Tangent(g7,g2) = 1.5708
FEATURE [PartDesign::Pocket] Pocket006
  BaseFeature = -> Fillet004
  Direction = (0,-7e-16,1)
  Length = 3
  Length2 = 5
  Placement = pos=(0,-2.9e-15,6.5) rot=(0,0,1;0rad)
  Profile = -> Sketch010
  ReferenceAxis = -> Sketch010 [N_Axis]
  Type = 0
FEATURE [Sketcher::SketchObject] Sketch011
  ExternalGeometry = -> [Fillet003]
  FullyConstrained = true
  MapMode = 5
  Placement = pos=(0,-1.5,-1.5) rot=(0,0.707107,-0.707107;3.14159rad)
  Support = -> [Fillet003]
  sketch-geometry (8):
    g0: LineSegment StartX=-32.4 StartY=-8 StartZ=0 EndX=-28.9 EndY=-8 EndZ=0
    g1: LineSegment StartX=-28.9 StartY=-8 StartZ=0 EndX=-28.9 EndY=1 EndZ=0
    g2: LineSegment StartX=-28.9 StartY=1 StartZ=0 EndX=-32.4 EndY=1 EndZ=0
    g3: LineSegment StartX=-32.4 StartY=1 StartZ=0 EndX=-32.4 EndY=-8 EndZ=0
    g4: LineSegment StartX=-1.4 StartY=-8 StartZ=0 EndX=-4.9 EndY=-8 EndZ=0
    g5: LineSegment StartX=-4.9 StartY=-8 StartZ=0 EndX=-4.9 EndY=1 EndZ=0
    g6: LineSegment StartX=-4.9 StartY=1 StartZ=0 EndX=-1.4 EndY=1 EndZ=0
    g7: LineSegment StartX=-1.4 StartY=1 StartZ=0 EndX=-1.4 EndY=-8 EndZ=0
  constraints (22):
    c: Coincident(g0,g1)
    c: Coincident(g1,g2)
    c: Coincident(g2,g3)
    c: Coincident(g3,g0)
    c: Horizontal(g0)
    c: Horizontal(g2)
    c: Vertical(g1)
    c: Vertical(g3)
    c: Coincident(g0,g-3)
    c: PointOnObject(g1,g-5)
    c: Coincident(g4,g5)
    c: Coincident(g5,g6)
    c: Coincident(g6,g7)
    c: Coincident(g7,g4)
    c: Horizontal(g4)
    c: Horizontal(g6)
    c: Vertical(g5)
    c: Vertical(g7)
    c: Coincident(g4,g-4)
    c: PointOnObject(g5,g-5)
    c: DistanceX(g2,g2) = 3.5
    c: Equal(g6,g2)
FEATURE [PartDesign::Pad] Pad005
  BaseFeature = -> Fillet003
  Direction = (0,-1,-4e-16)
  Length = 5
  Length2 = 10
  Placement = pos=(0,0,-1.5) rot=(1,0,0;3.14159rad)
  Profile = -> Sketch011
  ReferenceAxis = -> Sketch011 [N_Axis]
  Type = 0
FEATURE [PartDesign::Pad] Pad006
  BaseFeature = -> Pad005
  Direction = (0,1,6e-16)
  Length = 3
  Length2 = 10
  Placement = pos=(0,0,-1.5) rot=(1,0,0;3.14159rad)
  Profile = -> Pad005 [Face18]
  Type = 0
FEATURE [PartDesign::Pad] Pad007
  BaseFeature = -> Pad006
  Direction = (0,1,7e-16)
  Length = 3
  Length2 = 10
  Placement = pos=(0,0,-1.5) rot=(1,0,0;3.14159rad)
  Profile = -> Pad006 [Face21]
  Type = 0
FEATURE [PartDesign::Fillet] Fillet005
  Base = -> Pad007 [Edge78,Edge70,Edge166,Edge161]
  BaseFeature = -> Pad007
  Placement = pos=(0,0,-1.5) rot=(1,0,0;3.14159rad)
  Radius = 3
  SupportTransform = false
  UseAllEdges = false
FEATURE [Sketcher::SketchObject] Sketch012
  ExternalGeometry = -> [Fillet005]
  FullyConstrained = true
  MapMode = 5
  Placement = pos=(0,47.5,-1.5) rot=(-1,0,0;1.5708rad)
  Support = -> [Fillet005]
  sketch-geometry (8):
    g0: LineSegment StartX=1.4 StartY=-8 StartZ=0 EndX=4.9 EndY=-8 EndZ=0
    g1: LineSegment StartX=4.9 StartY=-8 StartZ=0 EndX=4.9 EndY=1 EndZ=0
    g2: LineSegment StartX=4.9 StartY=1 StartZ=0 EndX=1.4 EndY=1 EndZ=0
    g3: LineSegment StartX=1.4 StartY=1 StartZ=0 EndX=1.4 EndY=-8 EndZ=0
    g4: LineSegment StartX=32.4 StartY=-8 StartZ=0 EndX=28.9 EndY=-8 EndZ=0
    g5: LineSegment StartX=28.9 StartY=-8 StartZ=0 EndX=28.9 EndY=1 EndZ=0
    g6: LineSegment StartX=28.9 StartY=1 StartZ=0 EndX=32.4 EndY=1 EndZ=0
    g7: LineSegment StartX=32.4 StartY=1 StartZ=0 EndX=32.4 EndY=-8 EndZ=0
  constraints (22):
    c: Coincident(g0,g1)
    c: Coincident(g1,g2)
    c: Coincident(g2,g3)
    c: Coincident(g3,g0)
    c: Horizontal(g0)
    c: Horizontal(g2)
    c: Vertical(g1)
    c: Vertical(g3)
    c: Coincident(g0,g-4)
    c: PointOnObject(g1,g-3)
    c: Coincident(g4,g5)
    c: Coincident(g5,g6)
    c: Coincident(g6,g7)
    c: Coincident(g7,g4)
    c: Horizontal(g4)
    c: Horizontal(g6)
    c: Vertical(g5)
    c: Vertical(g7)
    c: Coincident(g4,g-5)
    c: PointOnObject(g5,g-3)
    c: DistanceX(g2,g2) = 3.5
    c: Equal(g6,g2)
FEATURE [PartDesign::Pad] Pad008
  BaseFeature = -> Fillet005
  Direction = (0,1,7e-16)
  Length = 5
  Length2 = 10
  Placement = pos=(0,0,-1.5) rot=(1,0,0;3.14159rad)
  Profile = -> Sketch012
  ReferenceAxis = -> Sketch012 [N_Axis]
  Type = 0
FEATURE [PartDesign::Pad] Pad009
  BaseFeature = -> Pad008
  Direction = (0,-1,-9e-16)
  Length = 3
  Length2 = 10
  Placement = pos=(0,0,-1.5) rot=(1,0,0;3.14159rad)
  Profile = -> Pad008 [Face68,Face67]
  Type = 0
FEATURE [PartDesign::Fillet] Fillet006
  Base = -> Pad009 [Edge247,Edge241,Edge143,Edge148]
  BaseFeature = -> Pad009
  Placement = pos=(0,0,-1.5) rot=(1,0,0;3.14159rad)
  Radius = 3
  SupportTransform = false
  UseAllEdges = false
FEATURE [PartDesign::Fillet] Fillet007
  Base = -> Fillet006 [Edge234,Edge247,Edge246,Edge244,Edge242,Edge213,Edge218,Edge217,Edge215,Edge226,Edge221,Edge225,Edge223,Edge239,Edge238,Edge236,Edge230,Edge228,Edge231,Edge229]
  BaseFeature = -> Fillet006
  Placement = pos=(0,0,-1.5) rot=(1,0,0;3.14159rad)
  Radius = 0.8
  SupportTransform = false
  UseAllEdges = false
FEATURE [Sketcher::SketchObject] Sketch014
  ExternalGeometry = -> [Fillet007]
  FullyConstrained = true
  MapMode = 5
  Placement = pos=(32.4,0,-1.5) rot=(0.57735,-0.57735,0.57735;4.18879rad)
  Support = -> [Fillet007]
  sketch-geometry (2):
    g0: Circle CenterX=4 CenterY=-3.5 CenterZ=0 NormalX=0 NormalY=0 NormalZ=1 AngleXU=0 Radius=0.6
    g1: Circle CenterX=-50 CenterY=-3.5 CenterZ=0 NormalX=0 NormalY=0 NormalZ=1 AngleXU=0 Radius=0.6
  constraints (6):
    c: Diameter(g0) = 1.2
    c: Equal(g1,g0)
    c: DistanceY(g0,g-3) = 1.5
    c: DistanceX(g0,g-3) = 2.5
    c: DistanceY(g1,g-4) = 1.5
    c: DistanceX(g-4,g1) = 2.5
FEATURE [PartDesign::Pocket] Pocket007
  BaseFeature = -> Fillet007
  Direction = (-1,0,0)
  Length = 5
  Length2 = 5
  Placement = pos=(0,0,-1.5) rot=(1,0,0;3.14159rad)
  Profile = -> Sketch014
  ReferenceAxis = -> Sketch014 [N_Axis]
  Type = 1
FEATURE [PartDesign::Pad] Pad010
  BaseFeature = -> Pocket007
  Direction = (0,-1.4e-15,1)
  Length = 1
  Length2 = 10
  Placement = pos=(0,0,-1.5) rot=(1,0,0;3.14159rad)
  Profile = -> Pocket007 [Face64]
  Type = 0
FEATURE [Sketcher::SketchObject] Sketch015
  ExternalGeometry = -> [Pad010]
  FullyConstrained = true
  MapMode = 5
  Placement = pos=(0,-1e-15,0.5) rot=(0,0,1;0rad)
  sketch-geometry (4):
    g0: LineSegment StartX=0.48 StartY=9.57 StartZ=0 EndX=33.31 EndY=9.57 EndZ=0
    g1: LineSegment StartX=33.31 StartY=9.57 StartZ=0 EndX=33.31 EndY=3.87 EndZ=0
    g2: LineSegment StartX=33.31 StartY=3.87 StartZ=0 EndX=0.48 EndY=3.87 EndZ=0
    g3: LineSegment StartX=0.48 StartY=3.87 StartZ=0 EndX=0.48 EndY=9.57 EndZ=0
  constraints (10):
    c: Coincident(g0,g1)
    c: Coincident(g1,g2)
    c: Coincident(g2,g3)
    c: Coincident(g3,g0)
    c: Horizontal(g2)
    c: Vertical(g1)
    c: Vertical(g3)
    c: Coincident(g0,g-3)
    c: DistanceY(g3,g3) = 5.7
    c: Coincident(g0,g-3)
FEATURE [PartDesign::Pocket] Pocket008
  BaseFeature = -> Pad010
  Direction = (0,0,-1)
  Length = 1.52
  Length2 = 5
  Placement = pos=(0,0,-1.5) rot=(1,0,0;3.14159rad)
  Profile = -> Sketch015
  ReferenceAxis = -> Sketch015 [N_Axis]
  Type = 0
FEATURE [PartDesign::ShapeBinder] ShapeBinder
  Support = -> [Part__Feature055]
  TraceSupport = false
FEATURE [Sketcher::SketchObject] Sketch016
  ExternalGeometry = -> [ShapeBinder]
  FullyConstrained = true
  MapMode = 5
  Placement = pos=(0,-1e-15,0.5) rot=(0,0,1;0rad)
  sketch-geometry (8):
    g0: ArcOfCircle CenterX=3.9 CenterY=42.96 CenterZ=0 NormalX=0 NormalY=0 NormalZ=1 AngleXU=0 Radius=0.8 StartAngle=1.5708 EndAngle=4.71239
    g1: ArcOfCircle CenterX=29.9 CenterY=42.96 CenterZ=0 NormalX=0 NormalY=0 NormalZ=1 AngleXU=0 Radius=0.8 StartAngle=4.71239 EndAngle=7.85398
    g2: LineSegment StartX=3.9 StartY=43.76 StartZ=0 EndX=29.9 EndY=43.76 EndZ=0
    g3: LineSegment StartX=29.9 StartY=42.16 StartZ=0 EndX=3.9 EndY=42.16 EndZ=0
    g4: ArcOfCircle CenterX=3.9 CenterY=3 CenterZ=0 NormalX=0 NormalY=0 NormalZ=1 AngleXU=0 Radius=0.8 StartAngle=1.5708 EndAngle=4.71239
    g5: ArcOfCircle CenterX=29.9 CenterY=3 CenterZ=0 NormalX=0 NormalY=0 NormalZ=1 AngleXU=0 Radius=0.8 StartAngle=4.71239 EndAngle=7.85398
    g6: LineSegment StartX=3.9 StartY=3.8 StartZ=0 EndX=29.9 EndY=3.8 EndZ=0
    g7: LineSegment StartX=29.9 StartY=2.2 StartZ=0 EndX=3.9 EndY=2.2 EndZ=0
  constraints (18):
    c: Coincident(g0,g-5)
    c: Diameter(g0) = 1.6
    c: Coincident(g1,g-6)
    c: Equal(g0,g1)
    c: Coincident(g2,g1)
    c: Horizontal(g2)
    c: Coincident(g3,g1)
    c: Horizontal(g3)
    c: Tangent(g3,g0) = 1.5708
    c: Tangent(g2,g0) = 1.5708
    c: Coincident(g4,g-8)
    c: Coincident(g5,g-10)
    c: Equal(g4,g5)
    c: Tangent(g7,g4) = 1.5708
    c: Tangent(g6,g4) = 1.5708
    c: Tangent(g6,g5) = 1.5708
    c: Tangent(g7,g5) = 1.5708
    c: Equal(g4,g0)
FEATURE [PartDesign::Pad] Pad011
  BaseFeature = -> Pocket008
  Direction = (0,-1e-15,1)
  Length = 4
  Length2 = 10
  Placement = pos=(0,0,-1.5) rot=(1,0,0;3.14159rad)
  Profile = -> Sketch016
  ReferenceAxis = -> Sketch016 [N_Axis]
  Type = 0
FEATURE [PartDesign::ShapeBinder] ShapeBinder001
  Support = -> [Pad011]
  TraceSupport = false
FEATURE [Sketcher::SketchObject] Sketch020
  FullyConstrained = false
  MapMode = 5
  Placement = pos=(0,-1.2e-14,4.5) rot=(0,0,1;0rad)
  sketch-geometry (6):
    g0: Circle CenterX=5.9 CenterY=42.96 CenterZ=0 NormalX=0 NormalY=0 NormalZ=1 AngleXU=0 Radius=0.9
    g1: Circle CenterX=27.9 CenterY=42.96 CenterZ=0 NormalX=0 NormalY=0 NormalZ=1 AngleXU=0 Radius=0.9
    g2: Circle CenterX=5.9 CenterY=3 CenterZ=0 NormalX=0 NormalY=0 NormalZ=1 AngleXU=0 Radius=0.9
    g3: Circle CenterX=27.9 CenterY=3 CenterZ=0 NormalX=0 NormalY=0 NormalZ=1 AngleXU=0 Radius=0.9
    g4: LineSegment StartX=3.9 StartY=3 StartZ=0 EndX=29.9 EndY=3 EndZ=0
    g5: LineSegment StartX=3.9 StartY=42.96 StartZ=0 EndX=29.9 EndY=42.96 EndZ=0
  constraints (12):
    c: PointOnObject(g1,g5)
    c: PointOnObject(g0,g5)
    c: PointOnObject(g2,g4)
    c: PointOnObject(g3,g4)
    c: DistanceX(g5,g0) = 2
    c: DistanceX(g1,g5) = 2
    c: DistanceX(g4,g2) = 2
    c: DistanceX(g3,g4) = 2
    c: Diameter(g0) = 1.8
    c: Equal(g0,g1)
    c: Equal(g1,g3)
    c: Equal(g3,g2)
FEATURE [PartDesign::Pocket] Pocket011
  BaseFeature = -> Pad011
  Direction = (0,2e-15,-1)
  Length = 3
  Length2 = 5
  Placement = pos=(0,0,-1.5) rot=(1,0,0;3.14159rad)
  Profile = -> Sketch020
  ReferenceAxis = -> Sketch020 [N_Axis]
  Type = 0
FEATURE [Sketcher::SketchObject] Sketch021
  FullyConstrained = false
  MapMode = 5
  Placement = pos=(0,-8e-15,6.5) rot=(1,0,0;3.14159rad)
  sketch-geometry (16):
    g0: ArcOfCircle CenterX=2.4 CenterY=-2.5 CenterZ=0 NormalX=0 NormalY=0 NormalZ=1 AngleXU=0 Radius=2.65 StartAngle=1.5708 EndAngle=3.1416
    g1: LineSegment StartX=2.4 StartY=0.15 StartZ=0 EndX=31.4 EndY=0.15 EndZ=0
    g2: ArcOfCircle CenterX=31.4 CenterY=-2.5 CenterZ=0 NormalX=0 NormalY=0 NormalZ=1 AngleXU=0 Radius=2.65 StartAngle=0 EndAngle=1.5708
    g3: LineSegment StartX=34.05 StartY=-2.5 StartZ=0 EndX=34.05 EndY=-43.5 EndZ=0
    g4: ArcOfCircle CenterX=31.4 CenterY=-43.5 CenterZ=0 NormalX=0 NormalY=0 NormalZ=1 AngleXU=0 Radius=2.65 StartAngle=4.71239 EndAngle=6.28319
    g5: LineSegment StartX=31.4 StartY=-46.15 StartZ=0 EndX=2.4 EndY=-46.15 EndZ=0
    g6: ArcOfCircle CenterX=2.4 CenterY=-43.5 CenterZ=0 NormalX=0 NormalY=0 NormalZ=1 AngleXU=0 Radius=2.65 StartAngle=3.14159 EndAngle=4.71239
    g7: LineSegment StartX=-0.25 StartY=-43.5 StartZ=0 EndX=-0.25 EndY=-2.50001 EndZ=0
    g8: ArcOfCircle CenterX=2.4 CenterY=-2.5 CenterZ=0 NormalX=0 NormalY=0 NormalZ=1 AngleXU=0 Radius=2 StartAngle=1.5708 EndAngle=3.14159
    g9: ArcOfCircle CenterX=31.4 CenterY=-2.5 CenterZ=0 NormalX=0 NormalY=0 NormalZ=1 AngleXU=0 Radius=2 StartAngle=0 EndAngle=1.5708
    g10: ArcOfCircle CenterX=31.4 CenterY=-43.5 CenterZ=0 NormalX=0 NormalY=0 NormalZ=1 AngleXU=0 Radius=2 StartAngle=4.71239 EndAngle=6.28319
    g11: ArcOfCircle CenterX=2.4 CenterY=-43.5 CenterZ=0 NormalX=0 NormalY=0 NormalZ=1 AngleXU=0 Radius=2 StartAngle=3.14159 EndAngle=4.71239
    g12: LineSegment StartX=2.4 StartY=-0.5 StartZ=0 EndX=31.4 EndY=-0.5 EndZ=0
    g13: LineSegment StartX=33.4 StartY=-2.5 StartZ=0 EndX=33.4 EndY=-43.5 EndZ=0
    g14: LineSegment StartX=31.4 StartY=-45.5 StartZ=0 EndX=2.4 EndY=-45.5 EndZ=0
    g15: LineSegment StartX=0.4 StartY=-43.5 StartZ=0 EndX=0.4 EndY=-2.5 EndZ=0
  constraints (27):
    c: Vertical(g3)
    c: Horizontal(g5)
    c: Coincident(g7,g0)
    c: Vertical(g7)
    c: Tangent(g1,g0) = 1.5708
    c: Tangent(g2,g1) = 1.5708
    c: Tangent(g3,g2) = 1.5708
    c: Tangent(g4,g3) = 1.5708
    c: Tangent(g5,g4) = 1.5708
    c: Tangent(g6,g5) = 1.5708
    c: Tangent(g7,g6) = 1.5708
    c: Coincident(g8,g0)
    c: Coincident(g9,g2)
    c: Coincident(g10,g4)
    c: Coincident(g11,g6)
    c: Coincident(g12,g8)
    c: Coincident(g12,g9)
    c: Horizontal(g12)
    c: Vertical(g13)
    c: Horizontal(g14)
    c: Vertical(g15)
    c: Tangent(g15,g8) = 1.5708
    c: Tangent(g15,g11) = 1.5708
    c: Tangent(g14,g11) = 1.5708
    c: Tangent(g14,g10) = 1.5708
    c: Tangent(g13,g10) = 1.5708
    c: Tangent(g13,g9) = 1.5708
FEATURE [PartDesign::Pad] Pad013
  BaseFeature = -> Pocket006
  Direction = (0,4e-15,-1)
  Length = 1
  Length2 = 10
  Placement = pos=(0,-2.9e-15,6.5) rot=(0,0,1;0rad)
  Profile = -> Sketch021
  ReferenceAxis = -> Sketch021 [N_Axis]
  Type = 0
FEATURE [Sketcher::SketchObject] Sketch022
  ExternalGeometry = -> [Pad013]
  FullyConstrained = true
  MapMode = 5
  Placement = pos=(0,-5.1e-15,9.5) rot=(1,0,0;3.14159rad)
  Support = -> [Pad013]
  sketch-geometry (9):
    g0: GeomPoint X=16.9 Y=-23 Z=0
    g1: LineSegment StartX=2.9 StartY=-10 StartZ=0 EndX=30.9 EndY=-10 EndZ=0
    g2: LineSegment StartX=30.9 StartY=-10 StartZ=0 EndX=30.9 EndY=-13 EndZ=0
    g3: LineSegment StartX=30.9 StartY=-13 StartZ=0 EndX=2.9 EndY=-13 EndZ=0
    g4: LineSegment StartX=2.9 StartY=-13 StartZ=0 EndX=2.9 EndY=-10 EndZ=0
    g5: LineSegment StartX=2.9 StartY=-33 StartZ=0 EndX=30.9 EndY=-33 EndZ=0
    g6: LineSegment StartX=30.9 StartY=-33 StartZ=0 EndX=30.9 EndY=-36 EndZ=0
    g7: LineSegment StartX=30.9 StartY=-36 StartZ=0 EndX=2.9 EndY=-36 EndZ=0
    g8: LineSegment StartX=2.9 StartY=-36 StartZ=0 EndX=2.9 EndY=-33 EndZ=0
  constraints (23):
    c: Coincident(g1,g2)
    c: Coincident(g2,g3)
    c: Coincident(g3,g4)
    c: Coincident(g4,g1)
    c: Horizontal(g1)
    c: Horizontal(g3)
    c: Vertical(g2)
    c: Vertical(g4)
    c: Coincident(g5,g6)
    c: Coincident(g6,g7)
    c: Coincident(g7,g8)
    c: Coincident(g8,g5)
    c: Horizontal(g7)
    c: Vertical(g6)
    c: Vertical(g8)
    c: DistanceX(g1,g1) = 28
    c: DistanceY(g2,g2) = 3
    c: Equal(g2,g6)
    c: Symmetric(g5,g2,g0)
    c: Symmetric(g5,g3,g0)
    c: DistanceX(g5,g3) = 0
    c: DistanceY(g5,g2) = 20
    c: Symmetric(g-3,g-4,g0)
FEATURE [PartDesign::Pad] Pad014
  BaseFeature = -> Pad013
  Direction = (0,1.5e-15,-1)
  Length = 3
  Length2 = 10
  Placement = pos=(0,-2.9e-15,6.5) rot=(0,0,1;0rad)
  Profile = -> Sketch022
  ReferenceAxis = -> Sketch022 [N_Axis]
  Type = 0
FEATURE [Sketcher::SketchObject] Sketch023
  ExternalGeometry = -> [Pad014]
  FullyConstrained = true
  MapMode = 5
  Placement = pos=(0,-5.1e-15,9.5) rot=(1,0,0;3.14159rad)
  Support = -> [Pad014]
  sketch-geometry (12):
    g0: ArcOfCircle CenterX=2.4 CenterY=-43.5 CenterZ=0 NormalX=0 NormalY=0 NormalZ=1 AngleXU=0 Radius=2 StartAngle=3.14159 EndAngle=4.71239
    g1: ArcOfCircle CenterX=31.4 CenterY=-43.5 CenterZ=0 NormalX=0 NormalY=0 NormalZ=1 AngleXU=0 Radius=2 StartAngle=4.71239 EndAngle=6.28319
    g2: ArcOfCircle CenterX=2.4 CenterY=-2.5 CenterZ=0 NormalX=0 NormalY=0 NormalZ=1 AngleXU=0 Radius=2 StartAngle=1.5708 EndAngle=3.14159
    g3: ArcOfCircle CenterX=31.4 CenterY=-2.5 CenterZ=0 NormalX=0 NormalY=0 NormalZ=1 AngleXU=0 Radius=2 StartAngle=0 EndAngle=1.5708
    g4: LineSegment StartX=2.4 StartY=-0.5 StartZ=0 EndX=31.4 EndY=-0.5 EndZ=0
    g5: LineSegment StartX=2.4 StartY=-45.5 StartZ=0 EndX=31.4 EndY=-45.5 EndZ=0
    g6: LineSegment StartX=0.4 StartY=-43.5 StartZ=0 EndX=0.4 EndY=-39.7 EndZ=0
    g7: LineSegment StartX=0.4 StartY=-39.7 StartZ=0 EndX=33.4 EndY=-39.7 EndZ=0
    g8: LineSegment StartX=33.4 StartY=-39.7 StartZ=0 EndX=33.4 EndY=-43.5 EndZ=0
    g9: LineSegment StartX=0.4 StartY=-2.5 StartZ=0 EndX=0.4 EndY=-6.3 EndZ=0
    g10: LineSegment StartX=0.4 StartY=-6.3 StartZ=0 EndX=33.4 EndY=-6.3 EndZ=0
    g11: LineSegment StartX=33.4 StartY=-6.3 StartZ=0 EndX=33.4 EndY=-2.5 EndZ=0
  constraints (32):
    c: Coincident(g0,g-6)
    c: Coincident(g0,g-6)
    c: Coincident(g0,g-7)
    c: Coincident(g1,g-8)
    c: Coincident(g1,g-8)
    c: Coincident(g1,g-8)
    c: Coincident(g2,g-5)
    c: Coincident(g2,g-5)
    c: Coincident(g2,g-5)
    c: Coincident(g3,g-3)
    c: Coincident(g3,g-4)
    c: Coincident(g3,g-3)
    c: Coincident(g4,g2)
    c: Coincident(g4,g3)
    c: Coincident(g5,g0)
    c: Coincident(g5,g1)
    c: Coincident(g6,g0)
    c: Vertical(g6)
    c: Coincident(g7,g6)
    c: Horizontal(g7)
    c: Coincident(g8,g7)
    c: Coincident(g8,g1)
    c: Vertical(g8)
    c: DistanceY(g8,g8) = 3.8
    c: Coincident(g9,g2)
    c: Vertical(g9)
    c: Coincident(g10,g9)
    c: Horizontal(g10)
    c: Coincident(g11,g10)
    c: Coincident(g11,g3)
    c: Vertical(g11)
    c: Equal(g11,g8)
FEATURE [PartDesign::Pad] Pad015
  BaseFeature = -> Pad014
  Direction = (0,1.8e-15,-1)
  Length = 4
  Length2 = 10
  Placement = pos=(0,-2.9e-15,6.5) rot=(0,0,1;0rad)
  Profile = -> Sketch023
  ReferenceAxis = -> Sketch023 [N_Axis]
  Type = 0
FEATURE [Sketcher::SketchObject] Sketch024
  ExternalGeometry = -> [ShapeBinder001]
  FullyConstrained = true
  MapMode = 5
  Placement = pos=(0,-1.1e-15,5.5) rot=(1,0,0;3.14159rad)
  Support = -> [Pad015]
  sketch-geometry (6):
    g0: Circle CenterX=5.9 CenterY=-42.96 CenterZ=0 NormalX=0 NormalY=0 NormalZ=1 AngleXU=0 Radius=1
    g1: Circle CenterX=27.9 CenterY=-42.96 CenterZ=0 NormalX=0 NormalY=0 NormalZ=1 AngleXU=0 Radius=1
    g2: Circle CenterX=5.9 CenterY=-3 CenterZ=0 NormalX=0 NormalY=0 NormalZ=1 AngleXU=0 Radius=1
    g3: Circle CenterX=27.9 CenterY=-3 CenterZ=0 NormalX=0 NormalY=0 NormalZ=1 AngleXU=0 Radius=1
    g4: LineSegment StartX=3.9 StartY=-42.96 StartZ=0 EndX=29.9 EndY=-42.96 EndZ=0
    g5: LineSegment StartX=3.9 StartY=-3 StartZ=0 EndX=29.9 EndY=-3 EndZ=0
  constraints (16):
    c: PointOnObject(g3,g5)
    c: PointOnObject(g2,g5)
    c: PointOnObject(g0,g4)
    c: PointOnObject(g1,g4)
    c: Diameter(g0) = 2
    c: Equal(g1,g0)
    c: Equal(g0,g2)
    c: Equal(g2,g3)
    c: DistanceX(g5,g2) = 2
    c: DistanceX(g3,g5) = 2
    c: DistanceX(g4,g0) = 2
    c: DistanceX(g1,g4) = 2
    c: Coincident(g5,g-3)
    c: Coincident(g5,g-4)
    c: Coincident(g4,g-5)
    c: Coincident(g4,g-6)
FEATURE [PartDesign::Pocket] Pocket012
  BaseFeature = -> Pad015
  Direction = (0,-2.2e-15,1)
  Length = 5
  Length2 = 5
  Placement = pos=(0,-2.9e-15,6.5) rot=(0,0,1;0rad)
  Profile = -> Sketch024
  ReferenceAxis = -> Sketch024 [N_Axis]
  Type = 1
FEATURE [Sketcher::SketchObject] Sketch025
  ExternalGeometry = -> [Pocket012]
  FullyConstrained = true
  MapMode = 5
  Placement = pos=(0,-4.3e-15,10.5) rot=(0,0,1;0rad)
  Support = -> [Pocket012]
  sketch-geometry (4):
    g0: Circle CenterX=5.9 CenterY=42.96 CenterZ=0 NormalX=0 NormalY=0 NormalZ=1 AngleXU=0 Radius=2.125
    g1: Circle CenterX=27.9 CenterY=42.96 CenterZ=0 NormalX=0 NormalY=0 NormalZ=1 AngleXU=0 Radius=2.125
    g2: Circle CenterX=5.9 CenterY=3 CenterZ=0 NormalX=0 NormalY=0 NormalZ=1 AngleXU=0 Radius=2.125
    g3: Circle CenterX=27.9 CenterY=3 CenterZ=0 NormalX=0 NormalY=0 NormalZ=1 AngleXU=0 Radius=2.125
  constraints (8):
    c: Coincident(g0,g-3)
    c: Coincident(g1,g-4)
    c: Coincident(g2,g-5)
    c: Coincident(g3,g-6)
    c: Diameter(g0) = 4.25
    c: Equal(g0,g1)
    c: Equal(g1,g3)
    c: Equal(g3,g2)
FEATURE [PartDesign::Pocket] Pocket013
  BaseFeature = -> Pocket012
  Direction = (0,2.6e-15,-1)
  Length = 3
  Length2 = 5
  Placement = pos=(0,-2.9e-15,6.5) rot=(0,0,1;0rad)
  Profile = -> Sketch025
  ReferenceAxis = -> Sketch025 [N_Axis]
  Type = 0
FEATURE [PartDesign::Fillet] Fillet009
  Base = -> Pocket013 [Edge136,Edge132,Edge131,Edge134,Edge139,Edge142,Edge140,Edge144]
  BaseFeature = -> Pocket013
  Placement = pos=(0,-2.9e-15,6.5) rot=(0,0,1;0rad)
  Radius = 1
  SupportTransform = false
  UseAllEdges = false
FEATURE [PartDesign::Body] Body002  label="Case_Bottom"
  Group = -> [DatumPlane001,ReferenceFillet003,Sketch009,Pad004,Fillet004,Sketch010,Pocket006,ShapeBinder001,Sketch021,Pad013,Sketch022,Pad014,Sketch023,Pad015,Sketch024,Pocket012,Sketch025,Pocket013,Fillet009]
  Origin = -> Origin115
  Tip = -> Fillet009
FEATURE [PartDesign::Pad] Pad016
  BaseFeature = -> Pocket011
  Direction = (0,-1.8e-15,1)
  Length = 0.4
  Length2 = 10
  Placement = pos=(0,0,-1.5) rot=(1,0,0;3.14159rad)
  Profile = -> Pocket011 [Face66]
  Type = 0
FEATURE [PartDesign::Pad] Pad018
  BaseFeature = -> Pad016
  Direction = (0,-1.4e-15,1)
  Length = 0.5
  Length2 = 10
  Placement = pos=(0,0,-1.5) rot=(1,0,0;3.14159rad)
  Profile = -> Pad016 [Face169,Face173,Face177,Face180,Face184,Face188]
  Type = 0
FEATURE [Part::Part2DObjectPython] ShapeString  # Draft 2D object (typed FeaturePython)
  FontFile = <userpath>/Téléchargements/ubuntu/Ubuntu-B.ttf
  MakeFace = true
  Placement = pos=(28.3629,3.34221,-2.5) rot=(0,1,0;3.14159rad)
  Size = 2.5
  String = Watchy
  Tracking = 0
FEATURE [Part::Extrusion] Extrude  label="Watchy"
  Base = -> ShapeString
  Dir = (0,0,-1)
  DirMode = 2
  FaceMakerClass = Part::FaceMakerBullseye
  LengthFwd = 0.5
  LengthRev = 0
  Placement = pos=(0.184744,0.772381,0.5) rot=(0,0,1;0rad)
  Solid = false
  Symmetric = false
FEATURE [PartDesign::ShapeBinder] ReferencePart__Feature055
  Support = -> [Part__Feature055]
  TraceSupport = false
FEATURE [PartDesign::Plane] DatumPlane002
  Length = 70.0989
  MapMode = 5
  Placement = pos=(0,0,1.6) rot=(0,0,1;0rad)
  ResizeMode = 0
  Support = -> [ReferencePart__Feature055]
  Width = 83.1771
FEATURE [Sketcher::SketchObject] Sketch026
  ExternalGeometry = -> [ReferencePart__Feature055]
  FullyConstrained = true
  MapMode = 5
  Placement = pos=(0,0,1.6) rot=(0,0,1;0rad)
  Support = -> [DatumPlane002]
  sketch-geometry (8):
    g0: ArcOfCircle CenterX=3.9 CenterY=42.96 CenterZ=0 NormalX=0 NormalY=0 NormalZ=1 AngleXU=0 Radius=1 StartAngle=1.5708 EndAngle=4.71239
    g1: ArcOfCircle CenterX=29.9 CenterY=42.96 CenterZ=0 NormalX=0 NormalY=0 NormalZ=1 AngleXU=0 Radius=1 StartAngle=4.71239 EndAngle=7.85398
    g2: LineSegment StartX=3.9 StartY=43.96 StartZ=0 EndX=29.9 EndY=43.96 EndZ=0
    g3: LineSegment StartX=29.9 StartY=41.96 StartZ=0 EndX=3.9 EndY=41.96 EndZ=0
    g4: ArcOfCircle CenterX=3.9 CenterY=42.96 CenterZ=0 NormalX=0 NormalY=0 NormalZ=1 AngleXU=0 Radius=2.5 StartAngle=1.5708 EndAngle=4.71239
    g5: ArcOfCircle CenterX=29.9 CenterY=42.96 CenterZ=0 NormalX=0 NormalY=0 NormalZ=1 AngleXU=0 Radius=2.5 StartAngle=4.71239 EndAngle=7.85398
    g6: LineSegment StartX=3.9 StartY=45.46 StartZ=0 EndX=29.9 EndY=45.46 EndZ=0
    g7: LineSegment StartX=3.9 StartY=40.46 StartZ=0 EndX=29.9 EndY=40.46 EndZ=0
  constraints (19):
    c: Coincident(g0,g-4)
    c: Coincident(g0,g-4)
    c: Coincident(g0,g-5)
    c: Coincident(g1,g-6)
    c: Coincident(g1,g-6)
    c: Coincident(g1,g-6)
    c: Coincident(g2,g0)
    c: Coincident(g2,g1)
    c: Coincident(g3,g1)
    c: Coincident(g3,g0)
    c: Coincident(g5,g1)
    c: Horizontal(g6)
    c: Horizontal(g7)
    c: DistanceY(g0,g4) = 1.5
    c: Tangent(g6,g4) = 1.5708
    c: Tangent(g6,g5) = 1.5708
    c: Tangent(g7,g5) = -1.5708
    c: Tangent(g7,g4) = -1.5708
    c: Coincident(g0,g4)
FEATURE [PartDesign::Pad] Pad019
  Direction = (0,0,1)
  Length = 3.5
  Length2 = 10
  Placement = pos=(0,0,1.6) rot=(0,0,1;0rad)
  Profile = -> Sketch026
  ReferenceAxis = -> Sketch026 [N_Axis]
  Type = 0
FEATURE [PartDesign::Body] Body003  label="Bride"
  Group = -> [DatumPlane002,ReferencePart__Feature055,Sketch026,Pad019]
  Origin = -> Origin116
  Tip = -> Pad019
FEATURE [PartDesign::FeatureBase] Clone
  BaseFeature = -> Body003
FEATURE [PartDesign::Body] Body004  label="Bride2"
  BaseFeature = -> Body003
  Group = -> [Clone]
  Origin = -> Origin117
  Placement = pos=(0,-40,0) rot=(0,0,1;0rad)
  Tip = -> Clone
FEATURE [Mesh::Feature] Micro_USB_Cover
  Placement = pos=(36.4,26.7,5) rot=(0.707107,-0.707107,0;3.14159rad)
FEATURE [Part::Feature] Micro_USB_Cover001
  shape: bbox 6 x 8.5 x 3.5 mm, 1068 faces, 0 solids (baked)
FEATURE [Sketcher::SketchObject] Sketch027
  FullyConstrained = true
  MapMode = 5
  Placement = pos=(0,0,0) rot=(0.57735,0.57735,0.57735;2.0944rad)
  Support = -> [YZ_Plane118]
  sketch-geometry (4):
    g0: LineSegment StartX=17.7 StartY=5.55 StartZ=0 EndX=27.2 EndY=5.55 EndZ=0
    g1: LineSegment StartX=27.2 StartY=5.55 StartZ=0 EndX=27.2 EndY=0.95 EndZ=0
    g2: LineSegment StartX=27.2 StartY=0.95 StartZ=0 EndX=17.7 EndY=0.95 EndZ=0
    g3: LineSegment StartX=17.7 StartY=0.95 StartZ=0 EndX=17.7 EndY=5.55 EndZ=0
  constraints (12):
    c: Coincident(g0,g1)
    c: Coincident(g1,g2)
    c: Coincident(g2,g3)
    c: Coincident(g3,g0)
    c: Horizontal(g0)
    c: Horizontal(g2)
    c: Vertical(g1)
    c: Vertical(g3)
    c: DistanceX(g0,g0) = 9.5
    c: DistanceY(g1,g1) = 4.6
    c: DistanceY(g-1,g2) = 0.95
    c: DistanceX(g-1,g2) = 17.7
FEATURE [PartDesign::Pad] Pad020
  Direction = (1,-2e-16,3e-16)
  Length = 2
  Length2 = 10
  Placement = pos=(0,0,0) rot=(0.57735,0.57735,0.57735;2.0944rad)
  Profile = -> Sketch027
  ReferenceAxis = -> Sketch027 [N_Axis]
  Type = 0
FEATURE [Part::Feature] Micro_USB_Cover001_solid  label="Micro_USB_Cover001 (Solid)"
  Placement = pos=(0.5,0,0) rot=(0,0,1;0rad)
  shape: bbox 6 x 8.5 x 3.5 mm, 1068 faces (baked)
FEATURE [PartDesign::ShapeBinder] ShapeBinder002
  Support = -> [Micro_USB_Cover001_solid]
  TraceSupport = false
FEATURE [PartDesign::Fillet] Fillet010
  Base = -> Pad020 [Edge1,Edge8,Edge5,Edge2,Edge4,Edge7,Edge10,Edge12]
  BaseFeature = -> Pad020
  Placement = pos=(0,0,0) rot=(0.57735,0.57735,0.57735;2.0944rad)
  Radius = 1
  SupportTransform = false
  UseAllEdges = false
FEATURE [PartDesign::Body] Body005
  Group = -> [Sketch027,Pad020,ShapeBinder002,Fillet010]
  Origin = -> Origin118
  Placement = pos=(35.4,0,0) rot=(0,0,1;0rad)
  Tip = -> Fillet010
FEATURE [Part::Fuse] Fusion  label="USB_Cap"
  Base = -> Body005
  Tool = -> Micro_USB_Cover001_solid
FEATURE [PartDesign::ShapeBinder] ShapeBinder003
  Placement = pos=(0,0,-2.5) rot=(1,0,0;3.14159rad)
  Support = -> [Sketch002]
  TraceSupport = false
FEATURE [Sketcher::SketchObject] Sketch028
  ExternalGeometry = -> [ShapeBinder003]
  FullyConstrained = true
  MapMode = 5
  Placement = pos=(0,0,-1.5) rot=(1,0,0;3.14159rad)
  Support = -> [Pocket]
  sketch-geometry (4):
    g0: LineSegment StartX=3 StartY=-12.3 StartZ=0 EndX=31 EndY=-12.3 EndZ=0
    g1: LineSegment StartX=31 StartY=-39.3 StartZ=0 EndX=31 EndY=-12.3 EndZ=0
    g2: LineSegment StartX=31 StartY=-39.3 StartZ=0 EndX=3 EndY=-39.3 EndZ=0
    g3: LineSegment StartX=3 StartY=-12.3 StartZ=0 EndX=3 EndY=-39.3 EndZ=0
  constraints (8):
    c: Coincident(g0,g-3)
    c: Coincident(g0,g-4)
    c: Coincident(g1,g-5)
    c: Coincident(g1,g0)
    c: Coincident(g2,g1)
    c: Coincident(g2,g-5)
    c: Coincident(g3,g0)
    c: Coincident(g3,g2)
FEATURE [PartDesign::Pad] Pad021
  BaseFeature = -> Pocket
  Direction = (0,0,-1)
  Length = 0.8
  Length2 = 10
  Profile = -> Sketch028
  ReferenceAxis = -> Sketch028 [N_Axis]
  Type = 0
FEATURE [PartDesign::Body] Body  label="Vitre"
  Group = -> [Sketch,Pad,Fillet,Pocket,ShapeBinder003,Sketch028,Pad021]
  Origin = -> Origin056
  Tip = -> Pad021
FEATURE [PartDesign::Pocket] Pocket014
  BaseFeature = -> Pad018
  Direction = (0,2.1e-15,-1)
  Length = 0.73
  Length2 = 5
  Placement = pos=(0,0,-1.5) rot=(1,0,0;3.14159rad)
  Profile = -> Pad018 [Face67]
  Type = 0
FEATURE [PartDesign::Pocket] Pocket015
  BaseFeature = -> Pocket014
  Direction = (0,2e-15,-1)
  Length = 0.33
  Length2 = 5
  Placement = pos=(0,0,-1.5) rot=(1,0,0;3.14159rad)
  Profile = -> Pocket014 [Face113,Face111,Face117,Face116]
  Type = 0
FEATURE [Sketcher::SketchObject] Sketch029
  ExternalGeometry = -> [Pocket015]
  FullyConstrained = true
  MapMode = 5
  Placement = pos=(0,-3e-16,0.65) rot=(0,0,1;0rad)
  Support = -> [Pocket015]
  sketch-geometry (4):
    g0: LineSegment StartX=34.7 StartY=26.9 StartZ=0 EndX=35.1 EndY=26.9 EndZ=0
    g1: LineSegment StartX=35.1 StartY=26.9 StartZ=0 EndX=35.1 EndY=18 EndZ=0
    g2: LineSegment StartX=35.1 StartY=18 StartZ=0 EndX=34.7 EndY=18 EndZ=0
    g3: LineSegment StartX=34.7 StartY=18 StartZ=0 EndX=34.7 EndY=26.9 EndZ=0
  constraints (12):
    c: Coincident(g0,g1)
    c: Coincident(g1,g2)
    c: Coincident(g2,g3)
    c: Coincident(g3,g0)
    c: Horizontal(g0)
    c: Horizontal(g2)
    c: Vertical(g1)
    c: Vertical(g3)
    c: DistanceX(g0,g0) = 0.4
    c: DistanceY(g-4,g0) = 1
    c: DistanceY(g1,g-4) = 1
    c: DistanceX(g-3,g0) = 0.3
FEATURE [PartDesign::Pad] Pad022
  BaseFeature = -> Pocket015
  Direction = (0,-1e-16,1)
  Length = 5
  Length2 = 10
  Placement = pos=(0,0,-1.5) rot=(1,0,0;3.14159rad)
  Profile = -> Sketch029
  ReferenceAxis = -> Sketch029 [N_Axis]
  Type = 0
FEATURE [PartDesign::Body] Body001  label="Case_Top"
  Group = -> [DatumPlane,ReferencePocket,Sketch001,Pad001,Sketch002,Pocket001,Sketch003,Pocket002,Sketch004,Pocket003,Sketch005,Pocket004,Sketch006,Pocket005,Sketch007,Pad002,Sketch008,Pad003,Fillet001,Fillet002,Fillet003,Sketch011,Pad005,Pad006,Pad007,Fillet005,Sketch012,Pad008,Pad009,Fillet006,Fillet007,Sketch014,Pocket007,Pad010,Sketch015,Pocket008,Sketch016,ShapeBinder,Pad011,Sketch020,Pocket011,Pad016,+5 more]
  Origin = -> Origin057
  Tip = -> Pad022
FEATURE [Part::Cut] Cut  label="Case_Top_Watchy"
  Base = -> Body001
  Tool = -> Extrude
